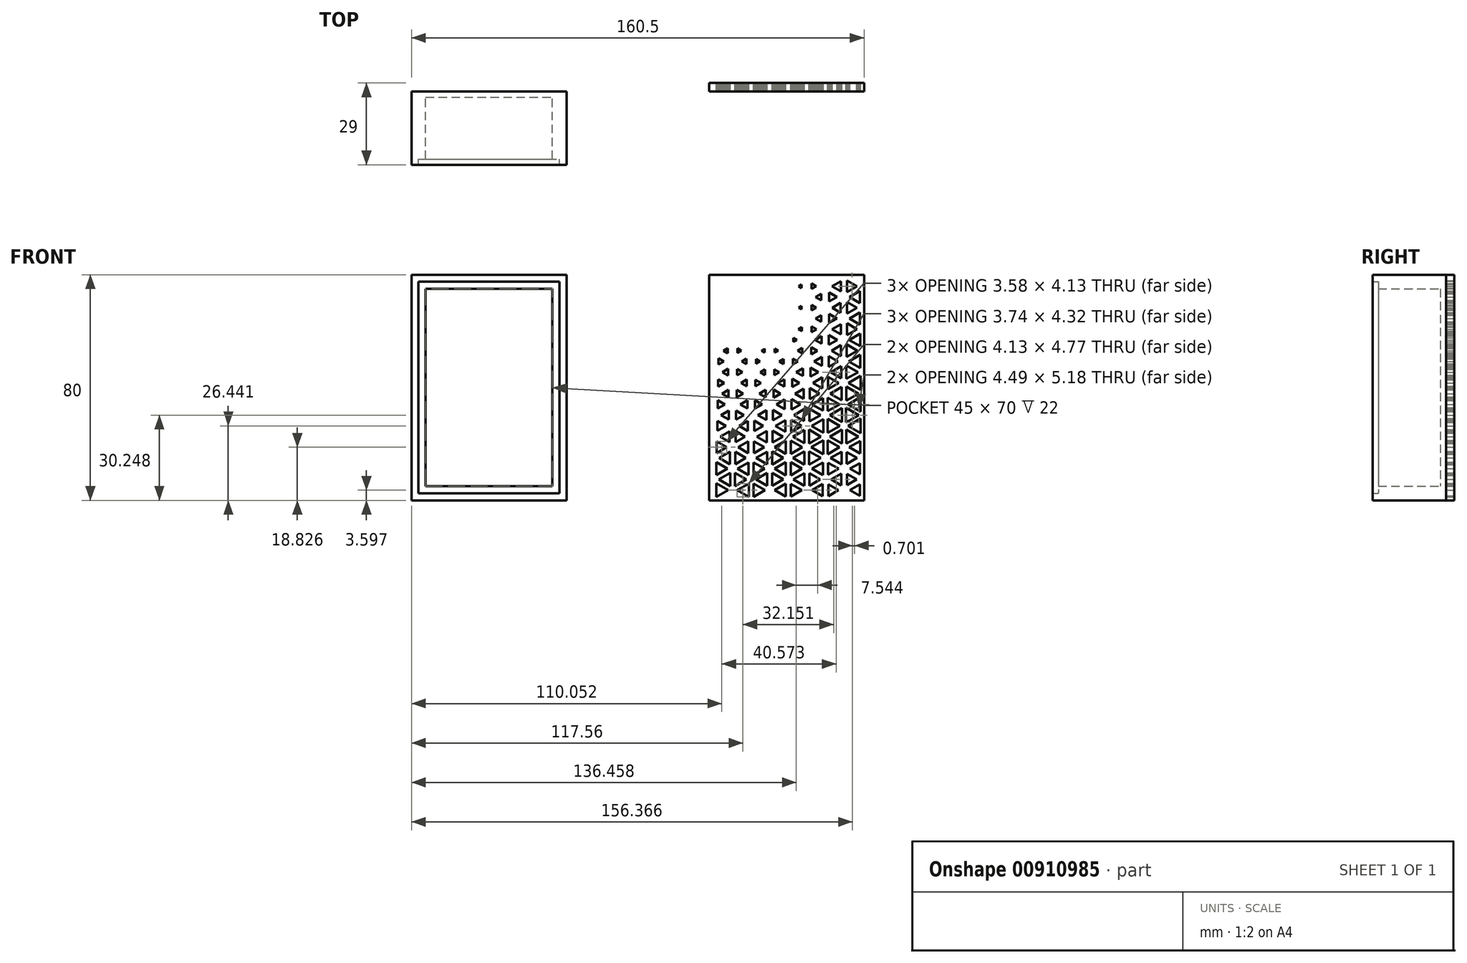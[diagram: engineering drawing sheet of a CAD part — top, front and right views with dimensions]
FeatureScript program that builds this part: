
annotation { "Feature Type Name" : "Feature", "Feature Type Description" : "" }
export const myFeature = defineFeature(function(context is Context, id is Id, definition is map)
    precondition{}
    {
        {
            var Q0;
            Q0=qCreatedBy(makeId("Front.planeOp"),FACE);
            var sketch = newSketch(context, id + "F0", { "sketchPlane" : qUnion([Q0])});
            skLineSegment(sketch, "E0.bottom", {"start": v(-84.52, 32) * mm, "end": v(-39.52, 32) * mm});
            skLineSegment(sketch, "E0.top", {"start": v(-84.52, -38) * mm, "end": v(-39.52, -38) * mm});
            skLineSegment(sketch, "E0.left", {"start": v(-84.52, 32) * mm, "end": v(-84.52, -38) * mm});
            skLineSegment(sketch, "E0.right", {"start": v(-39.52, 32) * mm, "end": v(-39.52, -38) * mm});
            skLineSegment(sketch, "E1.0", {"start": v(-89.52, 37) * mm, "end": v(-34.52, 37) * mm});
            skLineSegment(sketch, "E1.1", {"start": v(-89.52, 37) * mm, "end": v(-89.52, -43) * mm});
            skLineSegment(sketch, "E1.2", {"start": v(-89.52, -43) * mm, "end": v(-34.52, -43) * mm});
            skLineSegment(sketch, "E1.3", {"start": v(-34.52, 37) * mm, "end": v(-34.52, -43) * mm});
            skLineSegment(sketch, "E2.0", {"start": v(-37.02, 34.5) * mm, "end": v(-37.02, -40.5) * mm});
            skLineSegment(sketch, "E2.1", {"start": v(-87.02, 34.5) * mm, "end": v(-37.02, 34.5) * mm});
            skLineSegment(sketch, "E2.2", {"start": v(-87.02, 34.5) * mm, "end": v(-87.02, -40.5) * mm});
            skLineSegment(sketch, "E2.3", {"start": v(-87.02, -40.5) * mm, "end": v(-37.02, -40.5) * mm});
            skSolve(sketch);
        }
        {
            var Q0;
            Q0=makeQuery(id+"F0.imprint","IMPRINT",FACE,{"disambiguationData":[TD([[makeQuery(id+"F0.imprint","IMPRINT",EDGE,{"derivedFrom":sQuery(id+"F0.wireOp",EDGE,"E0.bottom")}),1.0]])]});
            extrude(context, id + "F1", {"entities" : qUnion([Q0]), "depth" : 22 * mm, "offsetDistance" : 25 * mm});
        }
        {
            var Q0;
            Q0=makeQuery(id+"F0.imprint","IMPRINT",FACE,{"disambiguationData":[TD([[makeQuery(id+"F0.imprint","IMPRINT",EDGE,{"derivedFrom":sQuery(id+"F0.wireOp",EDGE,"E1.0")}),-1.0]])]});
            extrude(context, id + "F2", {"entities" : qUnion([Q0]), "operationType" : NewBodyOperationType.ADD, "depth" : 24 * mm, "offsetDistance" : 25 * mm, "hasSecondDirection" : true, "secondDirectionOppositeDirection" : true, "secondDirectionDepth" : 2 * mm});
        }
        {
            var Q0;
            {var subQ0=sQuery(id+"F0.wireOp",EDGE,"E2.3");var subQ1=sQuery(id+"F0.wireOp",EDGE,"E2.2");var subQ2=sQuery(id+"F0.wireOp",EDGE,"E2.1");var subQ3=sQuery(id+"F0.wireOp",EDGE,"E2.0");Q0=makeQuery(id+"F2.boolean.opBoolean","SPLIT",FACE,{"disambiguationData":[TD([makeQuery(id+"F1.opExtrude","CAP_FACE",FACE,{"disambiguationData":[OSD([sQuery(id+"F0.wireOp",EDGE,"E0.bottom"),sQuery(id+"F0.wireOp",EDGE,"E0.top"),sQuery(id+"F0.wireOp",EDGE,"E0.left"),sQuery(id+"F0.wireOp",EDGE,"E0.right"),subQ3,subQ2,subQ1,subQ0])],"isStart":true})])],"derivedFrom":makeQuery(id+"F2.opExtrude","SWEPT_FACE",FACE,{"disambiguationData":[OSD([subQ1])]})});}
            extrude(context, id + "F3", {"entities" : qUnion([Q0]), "operationType" : NewBodyOperationType.ADD, "depth" : 51.4 * mm, "offsetDistance" : 25 * mm});
        }
        {
            var Q0;
            {var subQ0=sQuery(id+"F0.wireOp",EDGE,"E2.2");Q0=makeQuery(id+"F3.boolean.opBoolean","MERGE",FACE,{"derivedFrom":[makeQuery(id+"F2.opExtrude","CAP_FACE",FACE,{"disambiguationData":[OSD([sQuery(id+"F0.wireOp",EDGE,"E1.0"),sQuery(id+"F0.wireOp",EDGE,"E1.1"),sQuery(id+"F0.wireOp",EDGE,"E1.2"),sQuery(id+"F0.wireOp",EDGE,"E1.3"),sQuery(id+"F0.wireOp",EDGE,"E2.0"),sQuery(id+"F0.wireOp",EDGE,"E2.1"),subQ0,sQuery(id+"F0.wireOp",EDGE,"E2.3")])],"isStart":true}),makeQuery(id+"F3.opExtrude","SWEPT_FACE",FACE,{"disambiguationData":[OSD([subQ0]),TDD([makeQuery(id+"F2.opExtrude","CAP_EDGE",EDGE,{"disambiguationData":[OSD([subQ0])],"isStart":true})])]})]});}
            extrude(context, id + "F4", {"entities" : qUnion([Q0]), "depth" : 3 * mm, "offsetDistance" : 25 * mm});
        }
        {
            var Q0;
            Q0=makeQuery(id+"F4.opExtrude","SWEPT_BODY",BODY,{"disambiguationData":[OSD([sQuery(id+"F0.wireOp",EDGE,"E1.0"),sQuery(id+"F0.wireOp",EDGE,"E1.1"),sQuery(id+"F0.wireOp",EDGE,"E1.2"),sQuery(id+"F0.wireOp",EDGE,"E1.3"),sQuery(id+"F0.wireOp",EDGE,"E2.0"),sQuery(id+"F0.wireOp",EDGE,"E2.1"),sQuery(id+"F0.wireOp",EDGE,"E2.2"),sQuery(id+"F0.wireOp",EDGE,"E2.3")])]});
            transform(context, id + "F5", {"entities" : qUnion([Q0]), "transformType" : TransformType.TRANSLATION_3D, "dx" : 105.5 * mm, "dy" : 0 * mm, "dz" : 0 * mm, "makeCopy" : false});
        }
        {
            var Q0;
            Q0=makeQuery(id+"F4.opExtrude","CAP_FACE",FACE,{"disambiguationData":[OSD([sQuery(id+"F0.wireOp",EDGE,"E1.0"),sQuery(id+"F0.wireOp",EDGE,"E1.1"),sQuery(id+"F0.wireOp",EDGE,"E1.2"),sQuery(id+"F0.wireOp",EDGE,"E1.3"),sQuery(id+"F0.wireOp",EDGE,"E2.0"),sQuery(id+"F0.wireOp",EDGE,"E2.1"),sQuery(id+"F0.wireOp",EDGE,"E2.2"),sQuery(id+"F0.wireOp",EDGE,"E2.3")])],"isStart":false});
            var sketch = newSketch(context, id + "F6", { "sketchPlane" : qUnion([Q0])});
            skLineSegment(sketch, "E3", {"start": v(-19.2, -2.61) * mm, "end": v(-21.42, -1.33) * mm});
            skLineSegment(sketch, "E4", {"start": v(-21.42, -1.33) * mm, "end": v(-19.2, -0.05) * mm});
            skLineSegment(sketch, "E5", {"start": v(-19.2, -0.05) * mm, "end": v(-19.2, -2.61) * mm});
            skLineSegment(sketch, "E6", {"start": v(-19.3, 5.18) * mm, "end": v(-21.2, 6.29) * mm});
            skLineSegment(sketch, "E7", {"start": v(-21.2, 6.29) * mm, "end": v(-19.3, 7.39) * mm});
            skLineSegment(sketch, "E8", {"start": v(-19.3, 7.39) * mm, "end": v(-19.3, 5.18) * mm});
            skLineSegment(sketch, "E9", {"start": v(-20.78, 2.48) * mm, "end": v(-22.81, 1.3) * mm});
            skLineSegment(sketch, "E10", {"start": v(-22.81, 1.3) * mm, "end": v(-22.81, 3.65) * mm});
            skLineSegment(sketch, "E11", {"start": v(-22.81, 3.65) * mm, "end": v(-20.78, 2.48) * mm});
            skLineSegment(sketch, "E12", {"start": v(-20.58, -5.14) * mm, "end": v(-22.91, -6.49) * mm});
            skLineSegment(sketch, "E13", {"start": v(-22.91, -6.49) * mm, "end": v(-22.91, -3.79) * mm});
            skLineSegment(sketch, "E14", {"start": v(-22.91, -3.79) * mm, "end": v(-20.58, -5.14) * mm});
            skLineSegment(sketch, "E15", {"start": v(-21.1, 10.1) * mm, "end": v(-22.65, 9.2) * mm});
            skLineSegment(sketch, "E16", {"start": v(-22.65, 9.2) * mm, "end": v(-22.65, 11) * mm});
            skLineSegment(sketch, "E17", {"start": v(-22.65, 11) * mm, "end": v(-21.1, 10.1) * mm});
            skLineSegment(sketch, "E18", {"start": v(-25.9, 1.37) * mm, "end": v(-27.8, 2.48) * mm});
            skLineSegment(sketch, "E19", {"start": v(-27.8, 2.48) * mm, "end": v(-25.9, 3.58) * mm});
            skLineSegment(sketch, "E20", {"start": v(-25.9, 3.58) * mm, "end": v(-25.9, 1.37) * mm});
            skLineSegment(sketch, "E21", {"start": v(-19.09, -10.42) * mm, "end": v(-21.64, -8.94) * mm});
            skLineSegment(sketch, "E22", {"start": v(-21.64, -8.94) * mm, "end": v(-19.09, -7.47) * mm});
            skLineSegment(sketch, "E23", {"start": v(-19.09, -7.47) * mm, "end": v(-19.09, -10.42) * mm});
            skLineSegment(sketch, "E24", {"start": v(-26.06, 9.27) * mm, "end": v(-27.48, 10.1) * mm});
            skLineSegment(sketch, "E25", {"start": v(-27.48, 10.1) * mm, "end": v(-26.06, 10.91) * mm});
            skLineSegment(sketch, "E26", {"start": v(-26.06, 10.91) * mm, "end": v(-26.06, 9.27) * mm});
            skLineSegment(sketch, "E27", {"start": v(-27.65, 6.29) * mm, "end": v(-29.27, 5.35) * mm});
            skLineSegment(sketch, "E28", {"start": v(-29.27, 5.35) * mm, "end": v(-29.27, 7.22) * mm});
            skLineSegment(sketch, "E29", {"start": v(-29.27, 7.22) * mm, "end": v(-27.65, 6.29) * mm});
            skLineSegment(sketch, "E30", {"start": v(-27.37, -1.33) * mm, "end": v(-29.41, -2.51) * mm});
            skLineSegment(sketch, "E31", {"start": v(-29.41, -2.51) * mm, "end": v(-29.41, -0.15) * mm});
            skLineSegment(sketch, "E32", {"start": v(-29.41, -0.15) * mm, "end": v(-27.37, -1.33) * mm});
            skLineSegment(sketch, "E33", {"start": v(-25.76, -6.46) * mm, "end": v(-28.06, -5.14) * mm});
            skLineSegment(sketch, "E34", {"start": v(-28.06, -5.14) * mm, "end": v(-25.76, -3.8) * mm});
            skLineSegment(sketch, "E35", {"start": v(-25.76, -3.8) * mm, "end": v(-25.76, -6.46) * mm});
            skLineSegment(sketch, "E36", {"start": v(-25.6, -14.35) * mm, "end": v(-28.38, -12.75) * mm});
            skLineSegment(sketch, "E37", {"start": v(-28.38, -12.75) * mm, "end": v(-25.6, -11.15) * mm});
            skLineSegment(sketch, "E38", {"start": v(-25.6, -11.15) * mm, "end": v(-25.6, -14.35) * mm});
            skLineSegment(sketch, "E39", {"start": v(-20.28, -12.75) * mm, "end": v(-23.06, -14.36) * mm});
            skLineSegment(sketch, "E40", {"start": v(-23.06, -14.36) * mm, "end": v(-23.06, -11.15) * mm});
            skLineSegment(sketch, "E41", {"start": v(-23.06, -11.15) * mm, "end": v(-20.28, -12.75) * mm});
            skLineSegment(sketch, "E42", {"start": v(-32.63, 5.42) * mm, "end": v(-34.12, 6.29) * mm});
            skLineSegment(sketch, "E43", {"start": v(-34.12, 6.29) * mm, "end": v(-32.63, 7.15) * mm});
            skLineSegment(sketch, "E44", {"start": v(-32.63, 7.15) * mm, "end": v(-32.63, 5.42) * mm});
            skLineSegment(sketch, "E45", {"start": v(-34.17, 2.48) * mm, "end": v(-35.9, 1.48) * mm});
            skLineSegment(sketch, "E46", {"start": v(-35.9, 1.48) * mm, "end": v(-35.9, 3.48) * mm});
            skLineSegment(sketch, "E47", {"start": v(-35.9, 3.48) * mm, "end": v(-34.17, 2.48) * mm});
            skLineSegment(sketch, "E48", {"start": v(-32.46, -2.49) * mm, "end": v(-34.46, -1.33) * mm});
            skLineSegment(sketch, "E49", {"start": v(-34.46, -1.33) * mm, "end": v(-32.46, -0.17) * mm});
            skLineSegment(sketch, "E50", {"start": v(-32.46, -0.17) * mm, "end": v(-32.46, -2.49) * mm});
            skLineSegment(sketch, "E51", {"start": v(-27.04, -8.94) * mm, "end": v(-29.58, -10.41) * mm});
            skLineSegment(sketch, "E52", {"start": v(-29.58, -10.41) * mm, "end": v(-29.58, -7.48) * mm});
            skLineSegment(sketch, "E53", {"start": v(-29.58, -7.48) * mm, "end": v(-27.04, -8.94) * mm});
            skLineSegment(sketch, "E54", {"start": v(-26.67, -16.56) * mm, "end": v(-29.76, -18.34) * mm});
            skLineSegment(sketch, "E55", {"start": v(-29.76, -18.34) * mm, "end": v(-29.76, -14.78) * mm});
            skLineSegment(sketch, "E56", {"start": v(-29.76, -14.78) * mm, "end": v(-26.67, -16.56) * mm});
            skLineSegment(sketch, "E57", {"start": v(-18.92, -18.31) * mm, "end": v(-21.96, -16.56) * mm});
            skLineSegment(sketch, "E58", {"start": v(-21.96, -16.56) * mm, "end": v(-18.92, -14.8) * mm});
            skLineSegment(sketch, "E59", {"start": v(-18.92, -14.8) * mm, "end": v(-18.92, -18.31) * mm});
            skLineSegment(sketch, "E60", {"start": v(-34.54, 10.1) * mm, "end": v(-35.72, 9.4) * mm});
            skLineSegment(sketch, "E61", {"start": v(-35.72, 9.4) * mm, "end": v(-35.72, 10.78) * mm});
            skLineSegment(sketch, "E62", {"start": v(-35.72, 10.78) * mm, "end": v(-34.54, 10.1) * mm});
            skLineSegment(sketch, "E63", {"start": v(-39.13, 1.46) * mm, "end": v(-40.9, 2.48) * mm});
            skLineSegment(sketch, "E64", {"start": v(-40.9, 2.48) * mm, "end": v(-39.13, 3.5) * mm});
            skLineSegment(sketch, "E65", {"start": v(-39.13, 3.5) * mm, "end": v(-39.13, 1.46) * mm});
            skLineSegment(sketch, "E66", {"start": v(-33.77, -5.14) * mm, "end": v(-36.1, -6.49) * mm});
            skLineSegment(sketch, "E67", {"start": v(-36.1, -6.49) * mm, "end": v(-36.1, -3.79) * mm});
            skLineSegment(sketch, "E68", {"start": v(-36.1, -3.79) * mm, "end": v(-33.77, -5.14) * mm});
            skLineSegment(sketch, "E69", {"start": v(-32.26, -10.44) * mm, "end": v(-34.85, -8.94) * mm});
            skLineSegment(sketch, "E70", {"start": v(-34.85, -8.94) * mm, "end": v(-32.26, -7.45) * mm});
            skLineSegment(sketch, "E71", {"start": v(-32.26, -7.45) * mm, "end": v(-32.26, -10.44) * mm});
            skLineSegment(sketch, "E72", {"start": v(-25.42, -22.28) * mm, "end": v(-28.74, -20.37) * mm});
            skLineSegment(sketch, "E73", {"start": v(-28.74, -20.37) * mm, "end": v(-25.42, -18.45) * mm});
            skLineSegment(sketch, "E74", {"start": v(-25.42, -18.45) * mm, "end": v(-25.42, -22.28) * mm});
            skLineSegment(sketch, "E75", {"start": v(-19.94, -20.37) * mm, "end": v(-23.23, -22.27) * mm});
            skLineSegment(sketch, "E76", {"start": v(-23.23, -22.27) * mm, "end": v(-23.23, -18.46) * mm});
            skLineSegment(sketch, "E77", {"start": v(-23.23, -18.46) * mm, "end": v(-19.94, -20.37) * mm});
            skLineSegment(sketch, "E78", {"start": v(-39.33, 9.41) * mm, "end": v(-40.5, 10.1) * mm});
            skLineSegment(sketch, "E79", {"start": v(-40.5, 10.1) * mm, "end": v(-39.33, 10.77) * mm});
            skLineSegment(sketch, "E80", {"start": v(-39.33, 10.77) * mm, "end": v(-39.33, 9.41) * mm});
            skLineSegment(sketch, "E81", {"start": v(-40.9, 6.29) * mm, "end": v(-42.43, 5.4) * mm});
            skLineSegment(sketch, "E82", {"start": v(-42.43, 5.4) * mm, "end": v(-42.43, 7.16) * mm});
            skLineSegment(sketch, "E83", {"start": v(-42.43, 7.16) * mm, "end": v(-40.9, 6.29) * mm});
            skLineSegment(sketch, "E84", {"start": v(-40.44, -1.33) * mm, "end": v(-42.66, -2.61) * mm});
            skLineSegment(sketch, "E85", {"start": v(-42.66, -2.61) * mm, "end": v(-42.66, -0.05) * mm});
            skLineSegment(sketch, "E86", {"start": v(-42.66, -0.05) * mm, "end": v(-40.44, -1.33) * mm});
            skLineSegment(sketch, "E87", {"start": v(-38.9, -6.57) * mm, "end": v(-41.37, -5.14) * mm});
            skLineSegment(sketch, "E88", {"start": v(-41.37, -5.14) * mm, "end": v(-38.9, -3.7) * mm});
            skLineSegment(sketch, "E89", {"start": v(-38.9, -3.7) * mm, "end": v(-38.9, -6.57) * mm});
            skLineSegment(sketch, "E90", {"start": v(-33.35, -12.75) * mm, "end": v(-36.31, -14.46) * mm});
            skLineSegment(sketch, "E91", {"start": v(-36.31, -14.46) * mm, "end": v(-36.31, -11.04) * mm});
            skLineSegment(sketch, "E92", {"start": v(-36.31, -11.04) * mm, "end": v(-33.35, -12.75) * mm});
            skLineSegment(sketch, "E93", {"start": v(-32.07, -18.39) * mm, "end": v(-35.24, -16.56) * mm});
            skLineSegment(sketch, "E94", {"start": v(-35.24, -16.56) * mm, "end": v(-32.07, -14.73) * mm});
            skLineSegment(sketch, "E95", {"start": v(-32.07, -14.73) * mm, "end": v(-32.07, -18.39) * mm});
            skLineSegment(sketch, "E96", {"start": v(-31.9, -26.3) * mm, "end": v(-35.59, -24.17) * mm});
            skLineSegment(sketch, "E97", {"start": v(-35.59, -24.17) * mm, "end": v(-31.9, -22.04) * mm});
            skLineSegment(sketch, "E98", {"start": v(-31.9, -22.04) * mm, "end": v(-31.9, -26.3) * mm});
            skLineSegment(sketch, "E99", {"start": v(-26.32, -24.17) * mm, "end": v(-29.93, -26.26) * mm});
            skLineSegment(sketch, "E100", {"start": v(-29.93, -26.26) * mm, "end": v(-29.93, -22.1) * mm});
            skLineSegment(sketch, "E101", {"start": v(-29.93, -22.1) * mm, "end": v(-26.32, -24.17) * mm});
            skLineSegment(sketch, "E102", {"start": v(-18.74, -26.24) * mm, "end": v(-22.32, -24.17) * mm});
            skLineSegment(sketch, "E103", {"start": v(-22.32, -24.17) * mm, "end": v(-18.74, -22.1) * mm});
            skLineSegment(sketch, "E104", {"start": v(-18.74, -22.1) * mm, "end": v(-18.74, -26.24) * mm});
            skLineSegment(sketch, "E105", {"start": v(-45.72, 5.25) * mm, "end": v(-47.51, 6.29) * mm});
            skLineSegment(sketch, "E106", {"start": v(-47.51, 6.29) * mm, "end": v(-45.72, 7.32) * mm});
            skLineSegment(sketch, "E107", {"start": v(-45.72, 7.32) * mm, "end": v(-45.72, 5.25) * mm});
            skLineSegment(sketch, "E108", {"start": v(-46.95, 2.48) * mm, "end": v(-49.3, 1.12) * mm});
            skLineSegment(sketch, "E109", {"start": v(-49.3, 1.12) * mm, "end": v(-49.3, 3.83) * mm});
            skLineSegment(sketch, "E110", {"start": v(-49.3, 3.83) * mm, "end": v(-46.95, 2.48) * mm});
            skLineSegment(sketch, "E111", {"start": v(-45.48, -2.78) * mm, "end": v(-47.99, -1.33) * mm});
            skLineSegment(sketch, "E112", {"start": v(-47.99, -1.33) * mm, "end": v(-45.48, 0.12) * mm});
            skLineSegment(sketch, "E113", {"start": v(-45.48, 0.12) * mm, "end": v(-45.48, -2.78) * mm});
            skLineSegment(sketch, "E114", {"start": v(-39.96, -8.94) * mm, "end": v(-42.9, -10.64) * mm});
            skLineSegment(sketch, "E115", {"start": v(-42.9, -10.64) * mm, "end": v(-42.9, -7.25) * mm});
            skLineSegment(sketch, "E116", {"start": v(-42.9, -7.25) * mm, "end": v(-39.96, -8.94) * mm});
            skLineSegment(sketch, "E117", {"start": v(-38.68, -14.56) * mm, "end": v(-41.8, -12.75) * mm});
            skLineSegment(sketch, "E118", {"start": v(-41.8, -12.75) * mm, "end": v(-38.68, -10.95) * mm});
            skLineSegment(sketch, "E119", {"start": v(-38.68, -10.95) * mm, "end": v(-38.68, -14.56) * mm});
            skLineSegment(sketch, "E120", {"start": v(-32.98, -20.37) * mm, "end": v(-36.5, -22.4) * mm});
            skLineSegment(sketch, "E121", {"start": v(-36.5, -22.4) * mm, "end": v(-36.5, -18.33) * mm});
            skLineSegment(sketch, "E122", {"start": v(-36.5, -18.33) * mm, "end": v(-32.98, -20.37) * mm});
            skLineSegment(sketch, "E123", {"start": v(-32.73, -27.98) * mm, "end": v(-36.62, -30.22) * mm});
            skLineSegment(sketch, "E124", {"start": v(-36.62, -30.22) * mm, "end": v(-36.62, -25.74) * mm});
            skLineSegment(sketch, "E125", {"start": v(-36.62, -25.74) * mm, "end": v(-32.73, -27.98) * mm});
            skLineSegment(sketch, "E126", {"start": v(-25.27, -30.17) * mm, "end": v(-29.05, -27.98) * mm});
            skLineSegment(sketch, "E127", {"start": v(-29.05, -27.98) * mm, "end": v(-25.27, -25.8) * mm});
            skLineSegment(sketch, "E128", {"start": v(-25.27, -25.8) * mm, "end": v(-25.27, -30.17) * mm});
            skLineSegment(sketch, "E129", {"start": v(-19.62, -27.98) * mm, "end": v(-23.39, -30.16) * mm});
            skLineSegment(sketch, "E130", {"start": v(-23.39, -30.16) * mm, "end": v(-23.39, -25.8) * mm});
            skLineSegment(sketch, "E131", {"start": v(-23.39, -25.8) * mm, "end": v(-19.62, -27.98) * mm});
            skLineSegment(sketch, "E132", {"start": v(-45.9, 13.19) * mm, "end": v(-47.14, 13.9) * mm});
            skLineSegment(sketch, "E133", {"start": v(-47.14, 13.9) * mm, "end": v(-45.9, 14.61) * mm});
            skLineSegment(sketch, "E134", {"start": v(-45.9, 14.61) * mm, "end": v(-45.9, 13.19) * mm});
            skLineSegment(sketch, "E135", {"start": v(-47.39, 10.1) * mm, "end": v(-49.08, 9.12) * mm});
            skLineSegment(sketch, "E136", {"start": v(-49.08, 9.12) * mm, "end": v(-49.08, 11.07) * mm});
            skLineSegment(sketch, "E137", {"start": v(-49.08, 11.07) * mm, "end": v(-47.39, 10.1) * mm});
            skLineSegment(sketch, "E138", {"start": v(-51.98, 0.87) * mm, "end": v(-54.77, 2.48) * mm});
            skLineSegment(sketch, "E139", {"start": v(-54.77, 2.48) * mm, "end": v(-51.98, 4.09) * mm});
            skLineSegment(sketch, "E140", {"start": v(-51.98, 4.09) * mm, "end": v(-51.98, 0.87) * mm});
            skLineSegment(sketch, "E141", {"start": v(-46.47, -5.14) * mm, "end": v(-49.54, -6.9) * mm});
            skLineSegment(sketch, "E142", {"start": v(-49.54, -6.9) * mm, "end": v(-49.54, -3.37) * mm});
            skLineSegment(sketch, "E143", {"start": v(-49.54, -3.37) * mm, "end": v(-46.47, -5.14) * mm});
            skLineSegment(sketch, "E144", {"start": v(-45.24, -10.8) * mm, "end": v(-48.45, -8.94) * mm});
            skLineSegment(sketch, "E145", {"start": v(-48.45, -8.94) * mm, "end": v(-45.24, -7.1) * mm});
            skLineSegment(sketch, "E146", {"start": v(-45.24, -7.1) * mm, "end": v(-45.24, -10.8) * mm});
            skLineSegment(sketch, "E147", {"start": v(-39.57, -16.56) * mm, "end": v(-43.09, -18.59) * mm});
            skLineSegment(sketch, "E148", {"start": v(-43.09, -18.59) * mm, "end": v(-43.09, -14.53) * mm});
            skLineSegment(sketch, "E149", {"start": v(-43.09, -14.53) * mm, "end": v(-39.57, -16.56) * mm});
            skLineSegment(sketch, "E150", {"start": v(-38.5, -22.5) * mm, "end": v(-42.18, -20.37) * mm});
            skLineSegment(sketch, "E151", {"start": v(-42.18, -20.37) * mm, "end": v(-38.5, -18.24) * mm});
            skLineSegment(sketch, "E152", {"start": v(-38.5, -18.24) * mm, "end": v(-38.5, -22.5) * mm});
            skLineSegment(sketch, "E153", {"start": v(-31.82, -34.05) * mm, "end": v(-35.74, -31.79) * mm});
            skLineSegment(sketch, "E154", {"start": v(-35.74, -31.79) * mm, "end": v(-31.82, -29.53) * mm});
            skLineSegment(sketch, "E155", {"start": v(-31.82, -29.53) * mm, "end": v(-31.82, -34.05) * mm});
            skLineSegment(sketch, "E156", {"start": v(-26.13, -31.79) * mm, "end": v(-30.03, -34.04) * mm});
            skLineSegment(sketch, "E157", {"start": v(-30.03, -34.04) * mm, "end": v(-30.03, -29.54) * mm});
            skLineSegment(sketch, "E158", {"start": v(-30.03, -29.54) * mm, "end": v(-26.13, -31.79) * mm});
            skLineSegment(sketch, "E159", {"start": v(-18.62, -34.07) * mm, "end": v(-22.57, -31.79) * mm});
            skLineSegment(sketch, "E160", {"start": v(-22.57, -31.79) * mm, "end": v(-18.62, -29.5) * mm});
            skLineSegment(sketch, "E161", {"start": v(-18.62, -29.5) * mm, "end": v(-18.62, -34.07) * mm});
            skLineSegment(sketch, "E162", {"start": v(-47.68, 17.7) * mm, "end": v(-48.93, 16.98) * mm});
            skLineSegment(sketch, "E163", {"start": v(-48.93, 16.98) * mm, "end": v(-48.93, 18.43) * mm});
            skLineSegment(sketch, "E164", {"start": v(-48.93, 18.43) * mm, "end": v(-47.68, 17.7) * mm});
            skLineSegment(sketch, "E165", {"start": v(-52.18, 8.82) * mm, "end": v(-54.37, 10.1) * mm});
            skLineSegment(sketch, "E166", {"start": v(-54.37, 10.1) * mm, "end": v(-52.18, 11.36) * mm});
            skLineSegment(sketch, "E167", {"start": v(-52.18, 11.36) * mm, "end": v(-52.18, 8.82) * mm});
            skLineSegment(sketch, "E168", {"start": v(-53.27, 6.29) * mm, "end": v(-56.03, 4.7) * mm});
            skLineSegment(sketch, "E169", {"start": v(-56.03, 4.7) * mm, "end": v(-56.03, 7.88) * mm});
            skLineSegment(sketch, "E170", {"start": v(-56.03, 7.88) * mm, "end": v(-53.27, 6.29) * mm});
            skLineSegment(sketch, "E171", {"start": v(-52.89, -1.33) * mm, "end": v(-56.22, -3.25) * mm});
            skLineSegment(sketch, "E172", {"start": v(-56.22, -3.25) * mm, "end": v(-56.22, 0.6) * mm});
            skLineSegment(sketch, "E173", {"start": v(-56.22, 0.6) * mm, "end": v(-52.89, -1.33) * mm});
            skLineSegment(sketch, "E174", {"start": v(-51.76, -7.12) * mm, "end": v(-55.2, -5.14) * mm});
            skLineSegment(sketch, "E175", {"start": v(-55.2, -5.14) * mm, "end": v(-51.76, -3.16) * mm});
            skLineSegment(sketch, "E176", {"start": v(-51.76, -3.16) * mm, "end": v(-51.76, -7.12) * mm});
            skLineSegment(sketch, "E177", {"start": v(-46.1, -12.75) * mm, "end": v(-49.72, -14.85) * mm});
            skLineSegment(sketch, "E178", {"start": v(-49.72, -14.85) * mm, "end": v(-49.72, -10.65) * mm});
            skLineSegment(sketch, "E179", {"start": v(-49.72, -10.65) * mm, "end": v(-46.1, -12.75) * mm});
            skLineSegment(sketch, "E180", {"start": v(-45.07, -18.72) * mm, "end": v(-48.81, -16.56) * mm});
            skLineSegment(sketch, "E181", {"start": v(-48.81, -16.56) * mm, "end": v(-45.07, -14.4) * mm});
            skLineSegment(sketch, "E182", {"start": v(-45.07, -14.4) * mm, "end": v(-45.07, -18.72) * mm});
            skLineSegment(sketch, "E183", {"start": v(-39.27, -24.17) * mm, "end": v(-43.24, -26.46) * mm});
            skLineSegment(sketch, "E184", {"start": v(-43.24, -26.46) * mm, "end": v(-43.24, -21.88) * mm});
            skLineSegment(sketch, "E185", {"start": v(-43.24, -21.88) * mm, "end": v(-39.27, -24.17) * mm});
            skLineSegment(sketch, "E186", {"start": v(-38.4, -30.28) * mm, "end": v(-42.38, -27.98) * mm});
            skLineSegment(sketch, "E187", {"start": v(-42.38, -27.98) * mm, "end": v(-38.4, -25.68) * mm});
            skLineSegment(sketch, "E188", {"start": v(-38.4, -25.68) * mm, "end": v(-38.4, -30.28) * mm});
            skLineSegment(sketch, "E189", {"start": v(-38.4, -37.87) * mm, "end": v(-42.35, -35.6) * mm});
            skLineSegment(sketch, "E190", {"start": v(-42.35, -35.6) * mm, "end": v(-38.4, -33.32) * mm});
            skLineSegment(sketch, "E191", {"start": v(-38.4, -33.32) * mm, "end": v(-38.4, -37.87) * mm});
            skLineSegment(sketch, "E192", {"start": v(-32.68, -35.6) * mm, "end": v(-36.65, -37.89) * mm});
            skLineSegment(sketch, "E193", {"start": v(-36.65, -37.89) * mm, "end": v(-36.65, -33.3) * mm});
            skLineSegment(sketch, "E194", {"start": v(-36.65, -33.3) * mm, "end": v(-32.68, -35.6) * mm});
            skLineSegment(sketch, "E195", {"start": v(-25.19, -37.92) * mm, "end": v(-29.22, -35.6) * mm});
            skLineSegment(sketch, "E196", {"start": v(-29.22, -35.6) * mm, "end": v(-25.19, -33.27) * mm});
            skLineSegment(sketch, "E197", {"start": v(-25.19, -33.27) * mm, "end": v(-25.19, -37.92) * mm});
            skLineSegment(sketch, "E198", {"start": v(-19.42, -35.6) * mm, "end": v(-23.49, -37.94) * mm});
            skLineSegment(sketch, "E199", {"start": v(-23.49, -37.94) * mm, "end": v(-23.49, -33.25) * mm});
            skLineSegment(sketch, "E200", {"start": v(-23.49, -33.25) * mm, "end": v(-19.42, -35.6) * mm});
            skLineSegment(sketch, "E201", {"start": v(-47.83, 25.32) * mm, "end": v(-48.85, 24.73) * mm});
            skLineSegment(sketch, "E202", {"start": v(-48.85, 24.73) * mm, "end": v(-48.85, 25.91) * mm});
            skLineSegment(sketch, "E203", {"start": v(-48.85, 25.91) * mm, "end": v(-47.83, 25.32) * mm});
            skLineSegment(sketch, "E204", {"start": v(-52.31, 16.68) * mm, "end": v(-54.1, 17.7) * mm});
            skLineSegment(sketch, "E205", {"start": v(-54.1, 17.7) * mm, "end": v(-52.31, 18.74) * mm});
            skLineSegment(sketch, "E206", {"start": v(-52.31, 18.74) * mm, "end": v(-52.31, 16.68) * mm});
            skLineSegment(sketch, "E207", {"start": v(-53.59, 13.9) * mm, "end": v(-55.87, 12.59) * mm});
            skLineSegment(sketch, "E208", {"start": v(-55.87, 12.59) * mm, "end": v(-55.87, 15.21) * mm});
            skLineSegment(sketch, "E209", {"start": v(-55.87, 15.21) * mm, "end": v(-53.59, 13.9) * mm});
            skLineSegment(sketch, "E210", {"start": v(-58.4, 4.37) * mm, "end": v(-61.72, 6.29) * mm});
            skLineSegment(sketch, "E211", {"start": v(-61.72, 6.29) * mm, "end": v(-58.4, 8.2) * mm});
            skLineSegment(sketch, "E212", {"start": v(-58.4, 8.2) * mm, "end": v(-58.4, 4.37) * mm});
            skLineSegment(sketch, "E213", {"start": v(-59.2, 2.48) * mm, "end": v(-62.95, 0.32) * mm});
            skLineSegment(sketch, "E214", {"start": v(-62.95, 0.32) * mm, "end": v(-62.95, 4.64) * mm});
            skLineSegment(sketch, "E215", {"start": v(-62.95, 4.64) * mm, "end": v(-59.2, 2.48) * mm});
            skLineSegment(sketch, "E216", {"start": v(-58.25, -3.5) * mm, "end": v(-62, -1.33) * mm});
            skLineSegment(sketch, "E217", {"start": v(-62, -1.33) * mm, "end": v(-58.25, 0.84) * mm});
            skLineSegment(sketch, "E218", {"start": v(-58.25, 0.84) * mm, "end": v(-58.25, -3.5) * mm});
            skLineSegment(sketch, "E219", {"start": v(-52.54, -8.94) * mm, "end": v(-56.39, -11.16) * mm});
            skLineSegment(sketch, "E220", {"start": v(-56.39, -11.16) * mm, "end": v(-56.39, -6.73) * mm});
            skLineSegment(sketch, "E221", {"start": v(-56.39, -6.73) * mm, "end": v(-52.54, -8.94) * mm});
            skLineSegment(sketch, "E222", {"start": v(-51.6, -15.01) * mm, "end": v(-55.52, -12.75) * mm});
            skLineSegment(sketch, "E223", {"start": v(-55.52, -12.75) * mm, "end": v(-51.6, -10.5) * mm});
            skLineSegment(sketch, "E224", {"start": v(-51.6, -10.5) * mm, "end": v(-51.6, -15.01) * mm});
            skLineSegment(sketch, "E225", {"start": v(-45.81, -20.37) * mm, "end": v(-49.86, -22.7) * mm});
            skLineSegment(sketch, "E226", {"start": v(-49.86, -22.7) * mm, "end": v(-49.86, -18.03) * mm});
            skLineSegment(sketch, "E227", {"start": v(-49.86, -18.03) * mm, "end": v(-45.81, -20.37) * mm});
            skLineSegment(sketch, "E228", {"start": v(-44.95, -26.54) * mm, "end": v(-49.04, -24.17) * mm});
            skLineSegment(sketch, "E229", {"start": v(-49.04, -24.17) * mm, "end": v(-44.95, -21.81) * mm});
            skLineSegment(sketch, "E230", {"start": v(-44.95, -21.81) * mm, "end": v(-44.95, -26.54) * mm});
            skLineSegment(sketch, "E231", {"start": v(-39.25, -31.79) * mm, "end": v(-43.25, -34.1) * mm});
            skLineSegment(sketch, "E232", {"start": v(-43.25, -34.1) * mm, "end": v(-43.25, -29.48) * mm});
            skLineSegment(sketch, "E233", {"start": v(-43.25, -29.48) * mm, "end": v(-39.25, -31.79) * mm});
            skLineSegment(sketch, "E234", {"start": v(-39.28, -39.4) * mm, "end": v(-43.23, -41.68) * mm});
            skLineSegment(sketch, "E235", {"start": v(-43.23, -41.68) * mm, "end": v(-43.23, -37.12) * mm});
            skLineSegment(sketch, "E236", {"start": v(-43.23, -37.12) * mm, "end": v(-39.28, -39.4) * mm});
            skLineSegment(sketch, "E237", {"start": v(-31.77, -41.76) * mm, "end": v(-35.84, -39.4) * mm});
            skLineSegment(sketch, "E238", {"start": v(-35.84, -39.4) * mm, "end": v(-31.77, -37.05) * mm});
            skLineSegment(sketch, "E239", {"start": v(-31.77, -37.05) * mm, "end": v(-31.77, -41.76) * mm});
            skLineSegment(sketch, "E240", {"start": v(-25.98, -39.4) * mm, "end": v(-30.1, -41.79) * mm});
            skLineSegment(sketch, "E241", {"start": v(-30.1, -41.79) * mm, "end": v(-30.1, -37.02) * mm});
            skLineSegment(sketch, "E242", {"start": v(-30.1, -37.02) * mm, "end": v(-25.98, -39.4) * mm});
            skLineSegment(sketch, "E243", {"start": v(-18.55, -41.8) * mm, "end": v(-22.71, -39.4) * mm});
            skLineSegment(sketch, "E244", {"start": v(-22.71, -39.4) * mm, "end": v(-18.55, -37) * mm});
            skLineSegment(sketch, "E245", {"start": v(-18.55, -37) * mm, "end": v(-18.55, -41.8) * mm});
            skLineSegment(sketch, "E246", {"start": v(-47.8, 32.94) * mm, "end": v(-48.87, 32.32) * mm});
            skLineSegment(sketch, "E247", {"start": v(-48.87, 32.32) * mm, "end": v(-48.87, 33.55) * mm});
            skLineSegment(sketch, "E248", {"start": v(-48.87, 33.55) * mm, "end": v(-47.8, 32.94) * mm});
            skLineSegment(sketch, "E249", {"start": v(-52.38, 24.4) * mm, "end": v(-53.97, 25.32) * mm});
            skLineSegment(sketch, "E250", {"start": v(-53.97, 25.32) * mm, "end": v(-52.38, 26.25) * mm});
            skLineSegment(sketch, "E251", {"start": v(-52.38, 26.25) * mm, "end": v(-52.38, 24.4) * mm});
            skLineSegment(sketch, "E252", {"start": v(-53.77, 21.52) * mm, "end": v(-55.77, 20.36) * mm});
            skLineSegment(sketch, "E253", {"start": v(-55.77, 20.36) * mm, "end": v(-55.77, 22.67) * mm});
            skLineSegment(sketch, "E254", {"start": v(-55.77, 22.67) * mm, "end": v(-53.77, 21.52) * mm});
            skLineSegment(sketch, "E255", {"start": v(-58.52, 12.2) * mm, "end": v(-61.47, 13.9) * mm});
            skLineSegment(sketch, "E256", {"start": v(-61.47, 13.9) * mm, "end": v(-58.52, 15.6) * mm});
            skLineSegment(sketch, "E257", {"start": v(-58.52, 15.6) * mm, "end": v(-58.52, 12.2) * mm});
            skLineSegment(sketch, "E258", {"start": v(-59.45, 10.1) * mm, "end": v(-62.83, 8.14) * mm});
            skLineSegment(sketch, "E259", {"start": v(-62.83, 8.14) * mm, "end": v(-62.83, 12.04) * mm});
            skLineSegment(sketch, "E260", {"start": v(-62.83, 12.04) * mm, "end": v(-59.45, 10.1) * mm});
            skLineSegment(sketch, "E261", {"start": v(-64.74, 0.12) * mm, "end": v(-68.82, 2.48) * mm});
            skLineSegment(sketch, "E262", {"start": v(-68.82, 2.48) * mm, "end": v(-64.74, 4.83) * mm});
            skLineSegment(sketch, "E263", {"start": v(-64.74, 4.83) * mm, "end": v(-64.74, 0.12) * mm});
            skLineSegment(sketch, "E264", {"start": v(-58.96, -5.14) * mm, "end": v(-63.07, -7.51) * mm});
            skLineSegment(sketch, "E265", {"start": v(-63.07, -7.51) * mm, "end": v(-63.07, -2.76) * mm});
            skLineSegment(sketch, "E266", {"start": v(-63.07, -2.76) * mm, "end": v(-58.96, -5.14) * mm});
            skLineSegment(sketch, "E267", {"start": v(-58.13, -11.33) * mm, "end": v(-62.26, -8.94) * mm});
            skLineSegment(sketch, "E268", {"start": v(-62.26, -8.94) * mm, "end": v(-58.13, -6.56) * mm});
            skLineSegment(sketch, "E269", {"start": v(-58.13, -6.56) * mm, "end": v(-58.13, -11.33) * mm});
            skLineSegment(sketch, "E270", {"start": v(-52.32, -16.56) * mm, "end": v(-56.5, -18.97) * mm});
            skLineSegment(sketch, "E271", {"start": v(-56.5, -18.97) * mm, "end": v(-56.5, -14.14) * mm});
            skLineSegment(sketch, "E272", {"start": v(-56.5, -14.14) * mm, "end": v(-52.32, -16.56) * mm});
            skLineSegment(sketch, "E273", {"start": v(-51.5, -22.8) * mm, "end": v(-55.71, -20.37) * mm});
            skLineSegment(sketch, "E274", {"start": v(-55.71, -20.37) * mm, "end": v(-51.5, -17.94) * mm});
            skLineSegment(sketch, "E275", {"start": v(-51.5, -17.94) * mm, "end": v(-51.5, -22.8) * mm});
            skLineSegment(sketch, "E276", {"start": v(-45.77, -27.98) * mm, "end": v(-49.88, -30.36) * mm});
            skLineSegment(sketch, "E277", {"start": v(-49.88, -30.36) * mm, "end": v(-49.88, -25.6) * mm});
            skLineSegment(sketch, "E278", {"start": v(-49.88, -25.6) * mm, "end": v(-45.77, -27.98) * mm});
            skLineSegment(sketch, "E279", {"start": v(-44.98, -34.1) * mm, "end": v(-48.98, -31.79) * mm});
            skLineSegment(sketch, "E280", {"start": v(-48.98, -31.79) * mm, "end": v(-44.98, -29.48) * mm});
            skLineSegment(sketch, "E281", {"start": v(-44.98, -29.48) * mm, "end": v(-44.98, -34.1) * mm});
            skLineSegment(sketch, "E282", {"start": v(-38.36, -45.56) * mm, "end": v(-42.43, -43.21) * mm});
            skLineSegment(sketch, "E283", {"start": v(-42.43, -43.21) * mm, "end": v(-38.36, -40.86) * mm});
            skLineSegment(sketch, "E284", {"start": v(-38.36, -40.86) * mm, "end": v(-38.36, -45.56) * mm});
            skLineSegment(sketch, "E285", {"start": v(-32.57, -43.21) * mm, "end": v(-36.7, -45.6) * mm});
            skLineSegment(sketch, "E286", {"start": v(-36.7, -45.6) * mm, "end": v(-36.7, -40.82) * mm});
            skLineSegment(sketch, "E287", {"start": v(-36.7, -40.82) * mm, "end": v(-32.57, -43.21) * mm});
            skLineSegment(sketch, "E288", {"start": v(-25.1, -45.67) * mm, "end": v(-29.37, -43.21) * mm});
            skLineSegment(sketch, "E289", {"start": v(-29.37, -43.21) * mm, "end": v(-25.1, -40.75) * mm});
            skLineSegment(sketch, "E290", {"start": v(-25.1, -40.75) * mm, "end": v(-25.1, -45.67) * mm});
            skLineSegment(sketch, "E291", {"start": v(-19.3, -43.21) * mm, "end": v(-23.55, -45.66) * mm});
            skLineSegment(sketch, "E292", {"start": v(-23.55, -45.66) * mm, "end": v(-23.55, -40.76) * mm});
            skLineSegment(sketch, "E293", {"start": v(-23.55, -40.76) * mm, "end": v(-19.3, -43.21) * mm});
            skLineSegment(sketch, "E294", {"start": v(-45.86, 43.58) * mm, "end": v(-47.21, 44.36) * mm});
            skLineSegment(sketch, "E295", {"start": v(-47.21, 44.36) * mm, "end": v(-45.86, 45.14) * mm});
            skLineSegment(sketch, "E296", {"start": v(-45.86, 45.14) * mm, "end": v(-45.86, 43.58) * mm});
            skLineSegment(sketch, "E297", {"start": v(-47.58, 40.55) * mm, "end": v(-48.98, 39.74) * mm});
            skLineSegment(sketch, "E298", {"start": v(-48.98, 39.74) * mm, "end": v(-48.98, 41.36) * mm});
            skLineSegment(sketch, "E299", {"start": v(-48.98, 41.36) * mm, "end": v(-47.58, 40.55) * mm});
            skLineSegment(sketch, "E300", {"start": v(-52.35, 31.97) * mm, "end": v(-54.03, 32.94) * mm});
            skLineSegment(sketch, "E301", {"start": v(-54.03, 32.94) * mm, "end": v(-52.35, 33.9) * mm});
            skLineSegment(sketch, "E302", {"start": v(-52.35, 33.9) * mm, "end": v(-52.35, 31.97) * mm});
            skLineSegment(sketch, "E303", {"start": v(-53.79, 29.13) * mm, "end": v(-55.77, 27.99) * mm});
            skLineSegment(sketch, "E304", {"start": v(-55.77, 27.99) * mm, "end": v(-55.77, 30.27) * mm});
            skLineSegment(sketch, "E305", {"start": v(-55.77, 30.27) * mm, "end": v(-53.79, 29.13) * mm});
            skLineSegment(sketch, "E306", {"start": v(-58.6, 19.94) * mm, "end": v(-61.32, 21.52) * mm});
            skLineSegment(sketch, "E307", {"start": v(-61.32, 21.52) * mm, "end": v(-58.6, 23.1) * mm});
            skLineSegment(sketch, "E308", {"start": v(-58.6, 23.1) * mm, "end": v(-58.6, 19.94) * mm});
            skLineSegment(sketch, "E309", {"start": v(-59.62, 17.7) * mm, "end": v(-62.74, 15.9) * mm});
            skLineSegment(sketch, "E310", {"start": v(-62.74, 15.9) * mm, "end": v(-62.74, 19.5) * mm});
            skLineSegment(sketch, "E311", {"start": v(-62.74, 19.5) * mm, "end": v(-59.62, 17.7) * mm});
            skLineSegment(sketch, "E312", {"start": v(-64.83, 7.9) * mm, "end": v(-68.62, 10.1) * mm});
            skLineSegment(sketch, "E313", {"start": v(-68.62, 10.1) * mm, "end": v(-64.83, 12.28) * mm});
            skLineSegment(sketch, "E314", {"start": v(-64.83, 12.28) * mm, "end": v(-64.83, 7.9) * mm});
            skLineSegment(sketch, "E315", {"start": v(-65.6, 6.29) * mm, "end": v(-69.65, 3.95) * mm});
            skLineSegment(sketch, "E316", {"start": v(-69.65, 3.95) * mm, "end": v(-69.65, 8.62) * mm});
            skLineSegment(sketch, "E317", {"start": v(-69.65, 8.62) * mm, "end": v(-65.6, 6.29) * mm});
            skLineSegment(sketch, "E318", {"start": v(-65.43, -1.33) * mm, "end": v(-69.73, -3.81) * mm});
            skLineSegment(sketch, "E319", {"start": v(-69.73, -3.81) * mm, "end": v(-69.73, 1.15) * mm});
            skLineSegment(sketch, "E320", {"start": v(-69.73, 1.15) * mm, "end": v(-65.43, -1.33) * mm});
            skLineSegment(sketch, "E321", {"start": v(-64.66, -7.64) * mm, "end": v(-68.98, -5.14) * mm});
            skLineSegment(sketch, "E322", {"start": v(-68.98, -5.14) * mm, "end": v(-64.66, -2.64) * mm});
            skLineSegment(sketch, "E323", {"start": v(-64.66, -2.64) * mm, "end": v(-64.66, -7.64) * mm});
            skLineSegment(sketch, "E324", {"start": v(-58.8, -12.75) * mm, "end": v(-63.16, -15.27) * mm});
            skLineSegment(sketch, "E325", {"start": v(-63.16, -15.27) * mm, "end": v(-63.16, -10.23) * mm});
            skLineSegment(sketch, "E326", {"start": v(-63.16, -10.23) * mm, "end": v(-58.8, -12.75) * mm});
            skLineSegment(sketch, "E327", {"start": v(-58.05, -19.07) * mm, "end": v(-62.4, -16.56) * mm});
            skLineSegment(sketch, "E328", {"start": v(-62.4, -16.56) * mm, "end": v(-58.05, -14.05) * mm});
            skLineSegment(sketch, "E329", {"start": v(-58.05, -14.05) * mm, "end": v(-58.05, -19.07) * mm});
            skLineSegment(sketch, "E330", {"start": v(-52.28, -24.17) * mm, "end": v(-56.52, -26.62) * mm});
            skLineSegment(sketch, "E331", {"start": v(-56.52, -26.62) * mm, "end": v(-56.52, -21.73) * mm});
            skLineSegment(sketch, "E332", {"start": v(-56.52, -21.73) * mm, "end": v(-52.28, -24.17) * mm});
            skLineSegment(sketch, "E333", {"start": v(-51.54, -30.35) * mm, "end": v(-55.65, -27.98) * mm});
            skLineSegment(sketch, "E334", {"start": v(-55.65, -27.98) * mm, "end": v(-51.54, -25.61) * mm});
            skLineSegment(sketch, "E335", {"start": v(-51.54, -25.61) * mm, "end": v(-51.54, -30.35) * mm});
            skLineSegment(sketch, "E336", {"start": v(-45.94, -35.6) * mm, "end": v(-49.8, -37.83) * mm});
            skLineSegment(sketch, "E337", {"start": v(-49.8, -37.83) * mm, "end": v(-49.8, -33.36) * mm});
            skLineSegment(sketch, "E338", {"start": v(-49.8, -33.36) * mm, "end": v(-45.94, -35.6) * mm});
            skLineSegment(sketch, "E339", {"start": v(-45.02, -41.65) * mm, "end": v(-48.9, -39.4) * mm});
            skLineSegment(sketch, "E340", {"start": v(-48.9, -39.4) * mm, "end": v(-45.02, -37.16) * mm});
            skLineSegment(sketch, "E341", {"start": v(-45.02, -37.16) * mm, "end": v(-45.02, -41.65) * mm});
            skLineSegment(sketch, "E342", {"start": v(-44.98, -49.33) * mm, "end": v(-48.98, -47.02) * mm});
            skLineSegment(sketch, "E343", {"start": v(-48.98, -47.02) * mm, "end": v(-44.98, -44.71) * mm});
            skLineSegment(sketch, "E344", {"start": v(-44.98, -44.71) * mm, "end": v(-44.98, -49.33) * mm});
            skLineSegment(sketch, "E345", {"start": v(-39.2, -47.02) * mm, "end": v(-43.27, -49.37) * mm});
            skLineSegment(sketch, "E346", {"start": v(-43.27, -49.37) * mm, "end": v(-43.27, -44.67) * mm});
            skLineSegment(sketch, "E347", {"start": v(-43.27, -44.67) * mm, "end": v(-39.2, -47.02) * mm});
            skLineSegment(sketch, "E348", {"start": v(-31.71, -49.46) * mm, "end": v(-35.95, -47.02) * mm});
            skLineSegment(sketch, "E349", {"start": v(-35.95, -47.02) * mm, "end": v(-31.71, -44.57) * mm});
            skLineSegment(sketch, "E350", {"start": v(-31.71, -44.57) * mm, "end": v(-31.71, -49.46) * mm});
            skLineSegment(sketch, "E351", {"start": v(-25.87, -47.02) * mm, "end": v(-30.16, -49.5) * mm});
            skLineSegment(sketch, "E352", {"start": v(-30.16, -49.5) * mm, "end": v(-30.16, -44.54) * mm});
            skLineSegment(sketch, "E353", {"start": v(-30.16, -44.54) * mm, "end": v(-25.87, -47.02) * mm});
            skLineSegment(sketch, "E354", {"start": v(-18.53, -49.45) * mm, "end": v(-22.75, -47.02) * mm});
            skLineSegment(sketch, "E355", {"start": v(-22.75, -47.02) * mm, "end": v(-18.53, -44.58) * mm});
            skLineSegment(sketch, "E356", {"start": v(-18.53, -44.58) * mm, "end": v(-18.53, -49.45) * mm});
            skLineSegment(sketch, "E357", {"start": v(-41.02, 51.97) * mm, "end": v(-42.36, 51.2) * mm});
            skLineSegment(sketch, "E358", {"start": v(-42.36, 51.2) * mm, "end": v(-42.36, 52.75) * mm});
            skLineSegment(sketch, "E359", {"start": v(-42.36, 52.75) * mm, "end": v(-41.02, 51.97) * mm});
            skLineSegment(sketch, "E360", {"start": v(-45.68, 50.88) * mm, "end": v(-47.58, 51.97) * mm});
            skLineSegment(sketch, "E361", {"start": v(-47.58, 51.97) * mm, "end": v(-45.68, 53.07) * mm});
            skLineSegment(sketch, "E362", {"start": v(-45.68, 53.07) * mm, "end": v(-45.68, 50.88) * mm});
            skLineSegment(sketch, "E363", {"start": v(-47.22, 48.17) * mm, "end": v(-49.16, 47.05) * mm});
            skLineSegment(sketch, "E364", {"start": v(-49.16, 47.05) * mm, "end": v(-49.16, 49.29) * mm});
            skLineSegment(sketch, "E365", {"start": v(-49.16, 49.29) * mm, "end": v(-47.22, 48.17) * mm});
            skLineSegment(sketch, "E366", {"start": v(-52.23, 39.37) * mm, "end": v(-54.27, 40.55) * mm});
            skLineSegment(sketch, "E367", {"start": v(-54.27, 40.55) * mm, "end": v(-52.23, 41.73) * mm});
            skLineSegment(sketch, "E368", {"start": v(-52.23, 41.73) * mm, "end": v(-52.23, 39.37) * mm});
            skLineSegment(sketch, "E369", {"start": v(-53.64, 36.74) * mm, "end": v(-55.84, 35.48) * mm});
            skLineSegment(sketch, "E370", {"start": v(-55.84, 35.48) * mm, "end": v(-55.84, 38.01) * mm});
            skLineSegment(sketch, "E371", {"start": v(-55.84, 38.01) * mm, "end": v(-53.64, 36.74) * mm});
            skLineSegment(sketch, "E372", {"start": v(-58.6, 27.55) * mm, "end": v(-61.32, 29.13) * mm});
            skLineSegment(sketch, "E373", {"start": v(-61.32, 29.13) * mm, "end": v(-58.6, 30.7) * mm});
            skLineSegment(sketch, "E374", {"start": v(-58.6, 30.7) * mm, "end": v(-58.6, 27.55) * mm});
            skLineSegment(sketch, "E375", {"start": v(-59.68, 25.32) * mm, "end": v(-62.71, 23.57) * mm});
            skLineSegment(sketch, "E376", {"start": v(-62.71, 23.57) * mm, "end": v(-62.71, 27.07) * mm});
            skLineSegment(sketch, "E377", {"start": v(-62.71, 27.07) * mm, "end": v(-59.68, 25.32) * mm});
            skLineSegment(sketch, "E378", {"start": v(-64.9, 15.62) * mm, "end": v(-68.5, 17.7) * mm});
            skLineSegment(sketch, "E379", {"start": v(-68.5, 17.7) * mm, "end": v(-64.9, 19.8) * mm});
            skLineSegment(sketch, "E380", {"start": v(-64.9, 19.8) * mm, "end": v(-64.9, 15.62) * mm});
            skLineSegment(sketch, "E381", {"start": v(-65.73, 13.9) * mm, "end": v(-69.58, 11.68) * mm});
            skLineSegment(sketch, "E382", {"start": v(-69.58, 11.68) * mm, "end": v(-69.58, 16.12) * mm});
            skLineSegment(sketch, "E383", {"start": v(-69.58, 16.12) * mm, "end": v(-65.73, 13.9) * mm});
            skLineSegment(sketch, "E384", {"start": v(-65.3, -8.94) * mm, "end": v(-69.8, -11.54) * mm});
            skLineSegment(sketch, "E385", {"start": v(-69.8, -11.54) * mm, "end": v(-69.8, -6.35) * mm});
            skLineSegment(sketch, "E386", {"start": v(-69.8, -6.35) * mm, "end": v(-65.3, -8.94) * mm});
            skLineSegment(sketch, "E387", {"start": v(-64.6, -15.34) * mm, "end": v(-69.1, -12.75) * mm});
            skLineSegment(sketch, "E388", {"start": v(-69.1, -12.75) * mm, "end": v(-64.6, -10.16) * mm});
            skLineSegment(sketch, "E389", {"start": v(-64.6, -10.16) * mm, "end": v(-64.6, -15.34) * mm});
            skLineSegment(sketch, "E390", {"start": v(-58.8, -20.37) * mm, "end": v(-63.15, -22.87) * mm});
            skLineSegment(sketch, "E391", {"start": v(-63.15, -22.87) * mm, "end": v(-63.15, -17.86) * mm});
            skLineSegment(sketch, "E392", {"start": v(-63.15, -17.86) * mm, "end": v(-58.8, -20.37) * mm});
            skLineSegment(sketch, "E393", {"start": v(-58.1, -26.6) * mm, "end": v(-62.3, -24.17) * mm});
            skLineSegment(sketch, "E394", {"start": v(-62.3, -24.17) * mm, "end": v(-58.1, -21.76) * mm});
            skLineSegment(sketch, "E395", {"start": v(-58.1, -21.76) * mm, "end": v(-58.1, -26.6) * mm});
            skLineSegment(sketch, "E396", {"start": v(-52.53, -31.79) * mm, "end": v(-56.4, -34.02) * mm});
            skLineSegment(sketch, "E397", {"start": v(-56.4, -34.02) * mm, "end": v(-56.4, -29.56) * mm});
            skLineSegment(sketch, "E398", {"start": v(-56.4, -29.56) * mm, "end": v(-52.53, -31.79) * mm});
            skLineSegment(sketch, "E399", {"start": v(-51.64, -37.8) * mm, "end": v(-55.44, -35.6) * mm});
            skLineSegment(sketch, "E400", {"start": v(-55.44, -35.6) * mm, "end": v(-51.64, -33.4) * mm});
            skLineSegment(sketch, "E401", {"start": v(-51.64, -33.4) * mm, "end": v(-51.64, -37.8) * mm});
            skLineSegment(sketch, "E402", {"start": v(-45.9, -43.21) * mm, "end": v(-49.82, -45.47) * mm});
            skLineSegment(sketch, "E403", {"start": v(-49.82, -45.47) * mm, "end": v(-49.82, -40.95) * mm});
            skLineSegment(sketch, "E404", {"start": v(-49.82, -40.95) * mm, "end": v(-45.9, -43.21) * mm});
            skLineSegment(sketch, "E405", {"start": v(-52.06, 46.7) * mm, "end": v(-54.6, 48.17) * mm});
            skLineSegment(sketch, "E406", {"start": v(-54.6, 48.17) * mm, "end": v(-52.06, 49.63) * mm});
            skLineSegment(sketch, "E407", {"start": v(-52.06, 49.63) * mm, "end": v(-52.06, 46.7) * mm});
            skLineSegment(sketch, "E408", {"start": v(-53.36, 44.36) * mm, "end": v(-55.98, 42.85) * mm});
            skLineSegment(sketch, "E409", {"start": v(-55.98, 42.85) * mm, "end": v(-55.98, 45.87) * mm});
            skLineSegment(sketch, "E410", {"start": v(-55.98, 45.87) * mm, "end": v(-53.36, 44.36) * mm});
            skLineSegment(sketch, "E411", {"start": v(-58.54, 35.07) * mm, "end": v(-61.44, 36.74) * mm});
            skLineSegment(sketch, "E412", {"start": v(-61.44, 36.74) * mm, "end": v(-58.54, 38.42) * mm});
            skLineSegment(sketch, "E413", {"start": v(-58.54, 38.42) * mm, "end": v(-58.54, 35.07) * mm});
            skLineSegment(sketch, "E414", {"start": v(-59.63, 32.94) * mm, "end": v(-62.74, 31.14) * mm});
            skLineSegment(sketch, "E415", {"start": v(-62.74, 31.14) * mm, "end": v(-62.74, 34.73) * mm});
            skLineSegment(sketch, "E416", {"start": v(-62.74, 34.73) * mm, "end": v(-59.63, 32.94) * mm});
            skLineSegment(sketch, "E417", {"start": v(-64.92, 23.28) * mm, "end": v(-68.46, 25.32) * mm});
            skLineSegment(sketch, "E418", {"start": v(-68.46, 25.32) * mm, "end": v(-64.92, 27.37) * mm});
            skLineSegment(sketch, "E419", {"start": v(-64.92, 27.37) * mm, "end": v(-64.92, 23.28) * mm});
            skLineSegment(sketch, "E420", {"start": v(-65.81, 21.52) * mm, "end": v(-69.54, 19.36) * mm});
            skLineSegment(sketch, "E421", {"start": v(-69.54, 19.36) * mm, "end": v(-69.54, 23.67) * mm});
            skLineSegment(sketch, "E422", {"start": v(-69.54, 23.67) * mm, "end": v(-65.81, 21.52) * mm});
            skLineSegment(sketch, "E423", {"start": v(-65.33, -16.56) * mm, "end": v(-69.78, -19.13) * mm});
            skLineSegment(sketch, "E424", {"start": v(-69.78, -19.13) * mm, "end": v(-69.78, -13.99) * mm});
            skLineSegment(sketch, "E425", {"start": v(-69.78, -13.99) * mm, "end": v(-65.33, -16.56) * mm});
            skLineSegment(sketch, "E426", {"start": v(-64.67, -22.84) * mm, "end": v(-68.96, -20.37) * mm});
            skLineSegment(sketch, "E427", {"start": v(-68.96, -20.37) * mm, "end": v(-64.67, -17.9) * mm});
            skLineSegment(sketch, "E428", {"start": v(-64.67, -17.9) * mm, "end": v(-64.67, -22.84) * mm});
            skLineSegment(sketch, "E429", {"start": v(-59.13, -27.98) * mm, "end": v(-62.99, -30.21) * mm});
            skLineSegment(sketch, "E430", {"start": v(-62.99, -30.21) * mm, "end": v(-62.99, -25.75) * mm});
            skLineSegment(sketch, "E431", {"start": v(-62.99, -25.75) * mm, "end": v(-59.13, -27.98) * mm});
            skLineSegment(sketch, "E432", {"start": v(-58.27, -33.93) * mm, "end": v(-61.98, -31.79) * mm});
            skLineSegment(sketch, "E433", {"start": v(-61.98, -31.79) * mm, "end": v(-58.27, -29.64) * mm});
            skLineSegment(sketch, "E434", {"start": v(-58.27, -29.64) * mm, "end": v(-58.27, -33.93) * mm});
            skLineSegment(sketch, "E435", {"start": v(-52.61, -39.4) * mm, "end": v(-56.36, -41.57) * mm});
            skLineSegment(sketch, "E436", {"start": v(-56.36, -41.57) * mm, "end": v(-56.36, -37.24) * mm});
            skLineSegment(sketch, "E437", {"start": v(-56.36, -37.24) * mm, "end": v(-52.61, -39.4) * mm});
            skLineSegment(sketch, "E438", {"start": v(-51.63, -45.43) * mm, "end": v(-55.47, -43.21) * mm});
            skLineSegment(sketch, "E439", {"start": v(-55.47, -43.21) * mm, "end": v(-51.63, -41) * mm});
            skLineSegment(sketch, "E440", {"start": v(-51.63, -41) * mm, "end": v(-51.63, -45.43) * mm});
            skLineSegment(sketch, "E441", {"start": v(-53.1, 51.97) * mm, "end": v(-56.1, 50.24) * mm});
            skLineSegment(sketch, "E442", {"start": v(-56.1, 50.24) * mm, "end": v(-56.1, 53.71) * mm});
            skLineSegment(sketch, "E443", {"start": v(-56.1, 53.71) * mm, "end": v(-53.1, 51.97) * mm});
            skLineSegment(sketch, "E444", {"start": v(-58.45, 42.53) * mm, "end": v(-61.62, 44.36) * mm});
            skLineSegment(sketch, "E445", {"start": v(-61.62, 44.36) * mm, "end": v(-58.45, 46.2) * mm});
            skLineSegment(sketch, "E446", {"start": v(-58.45, 46.2) * mm, "end": v(-58.45, 42.53) * mm});
            skLineSegment(sketch, "E447", {"start": v(-59.51, 40.55) * mm, "end": v(-62.8, 38.66) * mm});
            skLineSegment(sketch, "E448", {"start": v(-62.8, 38.66) * mm, "end": v(-62.8, 42.45) * mm});
            skLineSegment(sketch, "E449", {"start": v(-62.8, 42.45) * mm, "end": v(-59.51, 40.55) * mm});
            skLineSegment(sketch, "E450", {"start": v(-64.9, 30.87) * mm, "end": v(-68.48, 32.94) * mm});
            skLineSegment(sketch, "E451", {"start": v(-68.48, 32.94) * mm, "end": v(-64.9, 35) * mm});
            skLineSegment(sketch, "E452", {"start": v(-64.9, 35) * mm, "end": v(-64.9, 30.87) * mm});
            skLineSegment(sketch, "E453", {"start": v(-65.82, 29.13) * mm, "end": v(-69.54, 26.98) * mm});
            skLineSegment(sketch, "E454", {"start": v(-69.54, 26.98) * mm, "end": v(-69.54, 31.28) * mm});
            skLineSegment(sketch, "E455", {"start": v(-69.54, 31.28) * mm, "end": v(-65.82, 29.13) * mm});
            skLineSegment(sketch, "E456", {"start": v(-65.68, -24.17) * mm, "end": v(-69.6, -26.44) * mm});
            skLineSegment(sketch, "E457", {"start": v(-69.6, -26.44) * mm, "end": v(-69.6, -21.9) * mm});
            skLineSegment(sketch, "E458", {"start": v(-69.6, -21.9) * mm, "end": v(-65.68, -24.17) * mm});
            skLineSegment(sketch, "E459", {"start": v(-64.87, -30.1) * mm, "end": v(-68.55, -27.98) * mm});
            skLineSegment(sketch, "E460", {"start": v(-68.55, -27.98) * mm, "end": v(-64.87, -25.85) * mm});
            skLineSegment(sketch, "E461", {"start": v(-64.87, -25.85) * mm, "end": v(-64.87, -30.1) * mm});
            skLineSegment(sketch, "E462", {"start": v(-59.31, -35.6) * mm, "end": v(-62.9, -37.66) * mm});
            skLineSegment(sketch, "E463", {"start": v(-62.9, -37.66) * mm, "end": v(-62.9, -33.53) * mm});
            skLineSegment(sketch, "E464", {"start": v(-62.9, -33.53) * mm, "end": v(-59.31, -35.6) * mm});
            skLineSegment(sketch, "E465", {"start": v(-58.28, -41.52) * mm, "end": v(-61.94, -39.4) * mm});
            skLineSegment(sketch, "E466", {"start": v(-61.94, -39.4) * mm, "end": v(-58.28, -37.29) * mm});
            skLineSegment(sketch, "E467", {"start": v(-58.28, -37.29) * mm, "end": v(-58.28, -41.52) * mm});
            skLineSegment(sketch, "E468", {"start": v(-52.55, -47.02) * mm, "end": v(-56.39, -49.24) * mm});
            skLineSegment(sketch, "E469", {"start": v(-56.39, -49.24) * mm, "end": v(-56.39, -44.8) * mm});
            skLineSegment(sketch, "E470", {"start": v(-56.39, -44.8) * mm, "end": v(-52.55, -47.02) * mm});
            skLineSegment(sketch, "E471", {"start": v(-58.37, 50.01) * mm, "end": v(-61.77, 51.97) * mm});
            skLineSegment(sketch, "E472", {"start": v(-61.77, 51.97) * mm, "end": v(-58.37, 53.93) * mm});
            skLineSegment(sketch, "E473", {"start": v(-58.37, 53.93) * mm, "end": v(-58.37, 50.01) * mm});
            skLineSegment(sketch, "E474", {"start": v(-59.39, 48.17) * mm, "end": v(-62.86, 46.16) * mm});
            skLineSegment(sketch, "E475", {"start": v(-62.86, 46.16) * mm, "end": v(-62.86, 50.17) * mm});
            skLineSegment(sketch, "E476", {"start": v(-62.86, 50.17) * mm, "end": v(-59.39, 48.17) * mm});
            skLineSegment(sketch, "E477", {"start": v(-64.88, 38.44) * mm, "end": v(-68.54, 40.55) * mm});
            skLineSegment(sketch, "E478", {"start": v(-68.54, 40.55) * mm, "end": v(-64.88, 42.66) * mm});
            skLineSegment(sketch, "E479", {"start": v(-64.88, 42.66) * mm, "end": v(-64.88, 38.44) * mm});
            skLineSegment(sketch, "E480", {"start": v(-65.79, 36.74) * mm, "end": v(-69.55, 34.57) * mm});
            skLineSegment(sketch, "E481", {"start": v(-69.55, 34.57) * mm, "end": v(-69.55, 38.92) * mm});
            skLineSegment(sketch, "E482", {"start": v(-69.55, 38.92) * mm, "end": v(-65.79, 36.74) * mm});
            skLineSegment(sketch, "E483", {"start": v(-66, -31.79) * mm, "end": v(-69.45, -33.78) * mm});
            skLineSegment(sketch, "E484", {"start": v(-69.45, -33.78) * mm, "end": v(-69.45, -29.8) * mm});
            skLineSegment(sketch, "E485", {"start": v(-69.45, -29.8) * mm, "end": v(-66, -31.79) * mm});
            skLineSegment(sketch, "E486", {"start": v(-64.94, -37.6) * mm, "end": v(-68.42, -35.6) * mm});
            skLineSegment(sketch, "E487", {"start": v(-68.42, -35.6) * mm, "end": v(-64.94, -33.59) * mm});
            skLineSegment(sketch, "E488", {"start": v(-64.94, -33.59) * mm, "end": v(-64.94, -37.6) * mm});
            skLineSegment(sketch, "E489", {"start": v(-59.24, -43.21) * mm, "end": v(-62.93, -45.34) * mm});
            skLineSegment(sketch, "E490", {"start": v(-62.93, -45.34) * mm, "end": v(-62.93, -41.08) * mm});
            skLineSegment(sketch, "E491", {"start": v(-62.93, -41.08) * mm, "end": v(-59.24, -43.21) * mm});
            skLineSegment(sketch, "E492", {"start": v(-58.25, -49.2) * mm, "end": v(-62.02, -47.02) * mm});
            skLineSegment(sketch, "E493", {"start": v(-62.02, -47.02) * mm, "end": v(-58.25, -44.84) * mm});
            skLineSegment(sketch, "E494", {"start": v(-58.25, -44.84) * mm, "end": v(-58.25, -49.2) * mm});
            skLineSegment(sketch, "E495", {"start": v(-64.86, 46.03) * mm, "end": v(-68.57, 48.17) * mm});
            skLineSegment(sketch, "E496", {"start": v(-68.57, 48.17) * mm, "end": v(-64.86, 50.3) * mm});
            skLineSegment(sketch, "E497", {"start": v(-64.86, 50.3) * mm, "end": v(-64.86, 46.03) * mm});
            skLineSegment(sketch, "E498", {"start": v(-65.77, 44.36) * mm, "end": v(-69.56, 42.17) * mm});
            skLineSegment(sketch, "E499", {"start": v(-69.56, 42.17) * mm, "end": v(-69.56, 46.55) * mm});
            skLineSegment(sketch, "E500", {"start": v(-69.56, 46.55) * mm, "end": v(-65.77, 44.36) * mm});
            skLineSegment(sketch, "E501", {"start": v(-65.95, -39.4) * mm, "end": v(-69.47, -41.44) * mm});
            skLineSegment(sketch, "E502", {"start": v(-69.47, -41.44) * mm, "end": v(-69.47, -37.37) * mm});
            skLineSegment(sketch, "E503", {"start": v(-69.47, -37.37) * mm, "end": v(-65.95, -39.4) * mm});
            skLineSegment(sketch, "E504", {"start": v(-64.89, -45.31) * mm, "end": v(-68.52, -43.21) * mm});
            skLineSegment(sketch, "E505", {"start": v(-68.52, -43.21) * mm, "end": v(-64.89, -41.11) * mm});
            skLineSegment(sketch, "E506", {"start": v(-64.89, -41.11) * mm, "end": v(-64.89, -45.31) * mm});
            skLineSegment(sketch, "E507", {"start": v(-65.78, 51.97) * mm, "end": v(-69.55, 49.8) * mm});
            skLineSegment(sketch, "E508", {"start": v(-69.55, 49.8) * mm, "end": v(-69.55, 54.15) * mm});
            skLineSegment(sketch, "E509", {"start": v(-69.55, 54.15) * mm, "end": v(-65.78, 51.97) * mm});
            skLineSegment(sketch, "E510", {"start": v(-65.87, -47.02) * mm, "end": v(-69.51, -49.12) * mm});
            skLineSegment(sketch, "E511", {"start": v(-69.51, -49.12) * mm, "end": v(-69.51, -44.91) * mm});
            skLineSegment(sketch, "E512", {"start": v(-69.51, -44.91) * mm, "end": v(-65.87, -47.02) * mm});
            skPoint(sketch, "E513", {"position": v(-69.8, -41.84) * mm});
            skSolve(sketch);
        }
        {
            var Q0;
            Q0=makeQuery(id+"F6.imprint","IMPRINT",FACE,{"disambiguationData":[TD([[makeQuery(id+"F6.imprint","IMPRINT",EDGE,{"derivedFrom":sQuery(id+"F6.wireOp",EDGE,"E396")}),-1.0]])]});
            var Q1;
            Q1=makeQuery(id+"F6.imprint","IMPRINT",FACE,{"disambiguationData":[TD([[makeQuery(id+"F6.imprint","IMPRINT",EDGE,{"derivedFrom":sQuery(id+"F6.wireOp",EDGE,"E420")}),-1.0]])]});
            var Q2;
            Q2=makeQuery(id+"F6.imprint","IMPRINT",FACE,{"disambiguationData":[TD([[makeQuery(id+"F6.imprint","IMPRINT",EDGE,{"derivedFrom":sQuery(id+"F6.wireOp",EDGE,"E120")}),-1.0]])]});
            var Q3;
            Q3=makeQuery(id+"F6.imprint","IMPRINT",FACE,{"disambiguationData":[TD([[makeQuery(id+"F6.imprint","IMPRINT",EDGE,{"derivedFrom":sQuery(id+"F6.wireOp",EDGE,"E12")}),-1.0]])]});
            var Q4;
            Q4=makeQuery(id+"F6.imprint","IMPRINT",FACE,{"disambiguationData":[TD([[makeQuery(id+"F6.imprint","IMPRINT",EDGE,{"derivedFrom":sQuery(id+"F6.wireOp",EDGE,"E168")}),-1.0]])]});
            var Q5;
            Q5=makeQuery(id+"F6.imprint","IMPRINT",FACE,{"disambiguationData":[TD([[makeQuery(id+"F6.imprint","IMPRINT",EDGE,{"derivedFrom":sQuery(id+"F6.wireOp",EDGE,"E456")}),-1.0]])]});
            var Q6;
            Q6=makeQuery(id+"F6.imprint","IMPRINT",FACE,{"disambiguationData":[TD([[makeQuery(id+"F6.imprint","IMPRINT",EDGE,{"derivedFrom":sQuery(id+"F6.wireOp",EDGE,"E15")}),-1.0]])]});
            var Q7;
            Q7=makeQuery(id+"F6.imprint","IMPRINT",FACE,{"disambiguationData":[TD([[makeQuery(id+"F6.imprint","IMPRINT",EDGE,{"derivedFrom":sQuery(id+"F6.wireOp",EDGE,"E231")}),-1.0]])]});
            var Q8;
            Q8=makeQuery(id+"F6.imprint","IMPRINT",FACE,{"disambiguationData":[TD([[makeQuery(id+"F6.imprint","IMPRINT",EDGE,{"derivedFrom":sQuery(id+"F6.wireOp",EDGE,"E417")}),-1.0]])]});
            var Q9;
            Q9=makeQuery(id+"F6.imprint","IMPRINT",FACE,{"disambiguationData":[TD([[makeQuery(id+"F6.imprint","IMPRINT",EDGE,{"derivedFrom":sQuery(id+"F6.wireOp",EDGE,"E150")}),-1.0]])]});
            var Q10;
            Q10=makeQuery(id+"F6.imprint","IMPRINT",FACE,{"disambiguationData":[TD([[makeQuery(id+"F6.imprint","IMPRINT",EDGE,{"derivedFrom":sQuery(id+"F6.wireOp",EDGE,"E24")}),-1.0]])]});
            var Q11;
            Q11=makeQuery(id+"F6.imprint","IMPRINT",FACE,{"disambiguationData":[TD([[makeQuery(id+"F6.imprint","IMPRINT",EDGE,{"derivedFrom":sQuery(id+"F6.wireOp",EDGE,"E165")}),-1.0]])]});
            var Q12;
            Q12=makeQuery(id+"F6.imprint","IMPRINT",FACE,{"disambiguationData":[TD([[makeQuery(id+"F6.imprint","IMPRINT",EDGE,{"derivedFrom":sQuery(id+"F6.wireOp",EDGE,"E93")}),-1.0]])]});
            var Q13;
            Q13=makeQuery(id+"F6.imprint","IMPRINT",FACE,{"disambiguationData":[TD([[makeQuery(id+"F6.imprint","IMPRINT",EDGE,{"derivedFrom":sQuery(id+"F6.wireOp",EDGE,"E3")}),-1.0]])]});
            var Q14;
            Q14=makeQuery(id+"F6.imprint","IMPRINT",FACE,{"disambiguationData":[TD([[makeQuery(id+"F6.imprint","IMPRINT",EDGE,{"derivedFrom":sQuery(id+"F6.wireOp",EDGE,"E390")}),-1.0]])]});
            var Q15;
            Q15=makeQuery(id+"F6.imprint","IMPRINT",FACE,{"disambiguationData":[TD([[makeQuery(id+"F6.imprint","IMPRINT",EDGE,{"derivedFrom":sQuery(id+"F6.wireOp",EDGE,"E114")}),-1.0]])]});
            var Q16;
            Q16=makeQuery(id+"F6.imprint","IMPRINT",FACE,{"disambiguationData":[TD([[makeQuery(id+"F6.imprint","IMPRINT",EDGE,{"derivedFrom":sQuery(id+"F6.wireOp",EDGE,"E75")}),-1.0]])]});
            var Q17;
            Q17=makeQuery(id+"F6.imprint","IMPRINT",FACE,{"disambiguationData":[TD([[makeQuery(id+"F6.imprint","IMPRINT",EDGE,{"derivedFrom":sQuery(id+"F6.wireOp",EDGE,"E207")}),-1.0]])]});
            var Q18;
            Q18=makeQuery(id+"F6.imprint","IMPRINT",FACE,{"disambiguationData":[TD([[makeQuery(id+"F6.imprint","IMPRINT",EDGE,{"derivedFrom":sQuery(id+"F6.wireOp",EDGE,"E57")}),-1.0]])]});
            var Q19;
            Q19=makeQuery(id+"F6.imprint","IMPRINT",FACE,{"disambiguationData":[TD([[makeQuery(id+"F6.imprint","IMPRINT",EDGE,{"derivedFrom":sQuery(id+"F6.wireOp",EDGE,"E33")}),-1.0]])]});
            var Q20;
            Q20=makeQuery(id+"F6.imprint","IMPRINT",FACE,{"disambiguationData":[TD([[makeQuery(id+"F6.imprint","IMPRINT",EDGE,{"derivedFrom":sQuery(id+"F6.wireOp",EDGE,"E90")}),-1.0]])]});
            var Q21;
            Q21=makeQuery(id+"F6.imprint","IMPRINT",FACE,{"disambiguationData":[TD([[makeQuery(id+"F6.imprint","IMPRINT",EDGE,{"derivedFrom":sQuery(id+"F6.wireOp",EDGE,"E141")}),-1.0]])]});
            var Q22;
            Q22=makeQuery(id+"F6.imprint","IMPRINT",FACE,{"disambiguationData":[TD([[makeQuery(id+"F6.imprint","IMPRINT",EDGE,{"derivedFrom":sQuery(id+"F6.wireOp",EDGE,"E126")}),-1.0]])]});
            var Q23;
            Q23=makeQuery(id+"F6.imprint","IMPRINT",FACE,{"disambiguationData":[TD([[makeQuery(id+"F6.imprint","IMPRINT",EDGE,{"derivedFrom":sQuery(id+"F6.wireOp",EDGE,"E111")}),-1.0]])]});
            var Q24;
            Q24=makeQuery(id+"F6.imprint","IMPRINT",FACE,{"disambiguationData":[TD([[makeQuery(id+"F6.imprint","IMPRINT",EDGE,{"derivedFrom":sQuery(id+"F6.wireOp",EDGE,"E375")}),-1.0]])]});
            var Q25;
            Q25=makeQuery(id+"F6.imprint","IMPRINT",FACE,{"disambiguationData":[TD([[makeQuery(id+"F6.imprint","IMPRINT",EDGE,{"derivedFrom":sQuery(id+"F6.wireOp",EDGE,"E249")}),-1.0]])]});
            var Q26;
            Q26=makeQuery(id+"F6.imprint","IMPRINT",FACE,{"disambiguationData":[TD([[makeQuery(id+"F6.imprint","IMPRINT",EDGE,{"derivedFrom":sQuery(id+"F6.wireOp",EDGE,"E426")}),-1.0]])]});
            var Q27;
            Q27=makeQuery(id+"F6.imprint","IMPRINT",FACE,{"disambiguationData":[TD([[makeQuery(id+"F6.imprint","IMPRINT",EDGE,{"derivedFrom":sQuery(id+"F6.wireOp",EDGE,"E330")}),-1.0]])]});
            var Q28;
            Q28=makeQuery(id+"F6.imprint","IMPRINT",FACE,{"disambiguationData":[TD([[makeQuery(id+"F6.imprint","IMPRINT",EDGE,{"derivedFrom":sQuery(id+"F6.wireOp",EDGE,"E138")}),-1.0]])]});
            var Q29;
            Q29=makeQuery(id+"F6.imprint","IMPRINT",FACE,{"disambiguationData":[TD([[makeQuery(id+"F6.imprint","IMPRINT",EDGE,{"derivedFrom":sQuery(id+"F6.wireOp",EDGE,"E177")}),-1.0]])]});
            var Q30;
            Q30=makeQuery(id+"F6.imprint","IMPRINT",FACE,{"disambiguationData":[TD([[makeQuery(id+"F6.imprint","IMPRINT",EDGE,{"derivedFrom":sQuery(id+"F6.wireOp",EDGE,"E54")}),-1.0]])]});
            var Q31;
            Q31=makeQuery(id+"F6.imprint","IMPRINT",FACE,{"disambiguationData":[TD([[makeQuery(id+"F6.imprint","IMPRINT",EDGE,{"derivedFrom":sQuery(id+"F6.wireOp",EDGE,"E384")}),-1.0]])]});
            var Q32;
            Q32=makeQuery(id+"F6.imprint","IMPRINT",FACE,{"disambiguationData":[TD([[makeQuery(id+"F6.imprint","IMPRINT",EDGE,{"derivedFrom":sQuery(id+"F6.wireOp",EDGE,"E45")}),-1.0]])]});
            var Q33;
            Q33=makeQuery(id+"F6.imprint","IMPRINT",FACE,{"disambiguationData":[TD([[makeQuery(id+"F6.imprint","IMPRINT",EDGE,{"derivedFrom":sQuery(id+"F6.wireOp",EDGE,"E336")}),-1.0]])]});
            var Q34;
            Q34=makeQuery(id+"F6.imprint","IMPRINT",FACE,{"disambiguationData":[TD([[makeQuery(id+"F6.imprint","IMPRINT",EDGE,{"derivedFrom":sQuery(id+"F6.wireOp",EDGE,"E36")}),-1.0]])]});
            var Q35;
            Q35=makeQuery(id+"F6.imprint","IMPRINT",FACE,{"disambiguationData":[TD([[makeQuery(id+"F6.imprint","IMPRINT",EDGE,{"derivedFrom":sQuery(id+"F6.wireOp",EDGE,"E213")}),-1.0]])]});
            var Q36;
            Q36=makeQuery(id+"F6.imprint","IMPRINT",FACE,{"disambiguationData":[TD([[makeQuery(id+"F6.imprint","IMPRINT",EDGE,{"derivedFrom":sQuery(id+"F6.wireOp",EDGE,"E315")}),-1.0]])]});
            var Q37;
            Q37=makeQuery(id+"F6.imprint","IMPRINT",FACE,{"disambiguationData":[TD([[makeQuery(id+"F6.imprint","IMPRINT",EDGE,{"derivedFrom":sQuery(id+"F6.wireOp",EDGE,"E162")}),-1.0]])]});
            var Q38;
            Q38=makeQuery(id+"F6.imprint","IMPRINT",FACE,{"disambiguationData":[TD([[makeQuery(id+"F6.imprint","IMPRINT",EDGE,{"derivedFrom":sQuery(id+"F6.wireOp",EDGE,"E300")}),-1.0]])]});
            var Q39;
            Q39=makeQuery(id+"F6.imprint","IMPRINT",FACE,{"disambiguationData":[TD([[makeQuery(id+"F6.imprint","IMPRINT",EDGE,{"derivedFrom":sQuery(id+"F6.wireOp",EDGE,"E267")}),-1.0]])]});
            var Q40;
            Q40=makeQuery(id+"F6.imprint","IMPRINT",FACE,{"disambiguationData":[TD([[makeQuery(id+"F6.imprint","IMPRINT",EDGE,{"derivedFrom":sQuery(id+"F6.wireOp",EDGE,"E18")}),-1.0]])]});
            var Q41;
            Q41=makeQuery(id+"F6.imprint","IMPRINT",FACE,{"disambiguationData":[TD([[makeQuery(id+"F6.imprint","IMPRINT",EDGE,{"derivedFrom":sQuery(id+"F6.wireOp",EDGE,"E378")}),-1.0]])]});
            var Q42;
            Q42=makeQuery(id+"F6.imprint","IMPRINT",FACE,{"disambiguationData":[TD([[makeQuery(id+"F6.imprint","IMPRINT",EDGE,{"derivedFrom":sQuery(id+"F6.wireOp",EDGE,"E81")}),-1.0]])]});
            var Q43;
            Q43=makeQuery(id+"F6.imprint","IMPRINT",FACE,{"disambiguationData":[TD([[makeQuery(id+"F6.imprint","IMPRINT",EDGE,{"derivedFrom":sQuery(id+"F6.wireOp",EDGE,"E39")}),-1.0]])]});
            var Q44;
            Q44=makeQuery(id+"F6.imprint","IMPRINT",FACE,{"disambiguationData":[TD([[makeQuery(id+"F6.imprint","IMPRINT",EDGE,{"derivedFrom":sQuery(id+"F6.wireOp",EDGE,"E147")}),-1.0]])]});
            var Q45;
            Q45=makeQuery(id+"F6.imprint","IMPRINT",FACE,{"disambiguationData":[TD([[makeQuery(id+"F6.imprint","IMPRINT",EDGE,{"derivedFrom":sQuery(id+"F6.wireOp",EDGE,"E309")}),-1.0]])]});
            var Q46;
            Q46=makeQuery(id+"F6.imprint","IMPRINT",FACE,{"disambiguationData":[TD([[makeQuery(id+"F6.imprint","IMPRINT",EDGE,{"derivedFrom":sQuery(id+"F6.wireOp",EDGE,"E273")}),-1.0]])]});
            var Q47;
            Q47=makeQuery(id+"F6.imprint","IMPRINT",FACE,{"disambiguationData":[TD([[makeQuery(id+"F6.imprint","IMPRINT",EDGE,{"derivedFrom":sQuery(id+"F6.wireOp",EDGE,"E393")}),-1.0]])]});
            var Q48;
            Q48=makeQuery(id+"F6.imprint","IMPRINT",FACE,{"disambiguationData":[TD([[makeQuery(id+"F6.imprint","IMPRINT",EDGE,{"derivedFrom":sQuery(id+"F6.wireOp",EDGE,"E189")}),-1.0]])]});
            var Q49;
            Q49=makeQuery(id+"F6.imprint","IMPRINT",FACE,{"disambiguationData":[TD([[makeQuery(id+"F6.imprint","IMPRINT",EDGE,{"derivedFrom":sQuery(id+"F6.wireOp",EDGE,"E312")}),-1.0]])]});
            var Q50;
            Q50=makeQuery(id+"F6.imprint","IMPRINT",FACE,{"disambiguationData":[TD([[makeQuery(id+"F6.imprint","IMPRINT",EDGE,{"derivedFrom":sQuery(id+"F6.wireOp",EDGE,"E381")}),-1.0]])]});
            var Q51;
            Q51=makeQuery(id+"F6.imprint","IMPRINT",FACE,{"disambiguationData":[TD([[makeQuery(id+"F6.imprint","IMPRINT",EDGE,{"derivedFrom":sQuery(id+"F6.wireOp",EDGE,"E30")}),-1.0]])]});
            var Q52;
            Q52=makeQuery(id+"F6.imprint","IMPRINT",FACE,{"disambiguationData":[TD([[makeQuery(id+"F6.imprint","IMPRINT",EDGE,{"derivedFrom":sQuery(id+"F6.wireOp",EDGE,"E216")}),-1.0]])]});
            var Q53;
            Q53=makeQuery(id+"F6.imprint","IMPRINT",FACE,{"disambiguationData":[TD([[makeQuery(id+"F6.imprint","IMPRINT",EDGE,{"derivedFrom":sQuery(id+"F6.wireOp",EDGE,"E333")}),-1.0]])]});
            var Q54;
            Q54=makeQuery(id+"F6.imprint","IMPRINT",FACE,{"disambiguationData":[TD([[makeQuery(id+"F6.imprint","IMPRINT",EDGE,{"derivedFrom":sQuery(id+"F6.wireOp",EDGE,"E222")}),-1.0]])]});
            var Q55;
            Q55=makeQuery(id+"F6.imprint","IMPRINT",FACE,{"disambiguationData":[TD([[makeQuery(id+"F6.imprint","IMPRINT",EDGE,{"derivedFrom":sQuery(id+"F6.wireOp",EDGE,"E183")}),-1.0]])]});
            var Q56;
            Q56=makeQuery(id+"F6.imprint","IMPRINT",FACE,{"disambiguationData":[TD([[makeQuery(id+"F6.imprint","IMPRINT",EDGE,{"derivedFrom":sQuery(id+"F6.wireOp",EDGE,"E429")}),-1.0]])]});
            var Q57;
            Q57=makeQuery(id+"F6.imprint","IMPRINT",FACE,{"disambiguationData":[TD([[makeQuery(id+"F6.imprint","IMPRINT",EDGE,{"derivedFrom":sQuery(id+"F6.wireOp",EDGE,"E21")}),-1.0]])]});
            var Q58;
            Q58=makeQuery(id+"F6.imprint","IMPRINT",FACE,{"disambiguationData":[TD([[makeQuery(id+"F6.imprint","IMPRINT",EDGE,{"derivedFrom":sQuery(id+"F6.wireOp",EDGE,"E432")}),-1.0]])]});
            var Q59;
            Q59=makeQuery(id+"F6.imprint","IMPRINT",FACE,{"disambiguationData":[TD([[makeQuery(id+"F6.imprint","IMPRINT",EDGE,{"derivedFrom":sQuery(id+"F6.wireOp",EDGE,"E303")}),-1.0]])]});
            var Q60;
            Q60=makeQuery(id+"F6.imprint","IMPRINT",FACE,{"disambiguationData":[TD([[makeQuery(id+"F6.imprint","IMPRINT",EDGE,{"derivedFrom":sQuery(id+"F6.wireOp",EDGE,"E69")}),-1.0]])]});
            var Q61;
            Q61=makeQuery(id+"F6.imprint","IMPRINT",FACE,{"disambiguationData":[TD([[makeQuery(id+"F6.imprint","IMPRINT",EDGE,{"derivedFrom":sQuery(id+"F6.wireOp",EDGE,"E159")}),-1.0]])]});
            var Q62;
            Q62=makeQuery(id+"F6.imprint","IMPRINT",FACE,{"disambiguationData":[TD([[makeQuery(id+"F6.imprint","IMPRINT",EDGE,{"derivedFrom":sQuery(id+"F6.wireOp",EDGE,"E327")}),-1.0]])]});
            var Q63;
            Q63=makeQuery(id+"F6.imprint","IMPRINT",FACE,{"disambiguationData":[TD([[makeQuery(id+"F6.imprint","IMPRINT",EDGE,{"derivedFrom":sQuery(id+"F6.wireOp",EDGE,"E105")}),-1.0]])]});
            var Q64;
            Q64=makeQuery(id+"F6.imprint","IMPRINT",FACE,{"disambiguationData":[TD([[makeQuery(id+"F6.imprint","IMPRINT",EDGE,{"derivedFrom":sQuery(id+"F6.wireOp",EDGE,"E48")}),-1.0]])]});
            var Q65;
            Q65=makeQuery(id+"F6.imprint","IMPRINT",FACE,{"disambiguationData":[TD([[makeQuery(id+"F6.imprint","IMPRINT",EDGE,{"derivedFrom":sQuery(id+"F6.wireOp",EDGE,"E210")}),-1.0]])]});
            var Q66;
            Q66=makeQuery(id+"F6.imprint","IMPRINT",FACE,{"disambiguationData":[TD([[makeQuery(id+"F6.imprint","IMPRINT",EDGE,{"derivedFrom":sQuery(id+"F6.wireOp",EDGE,"E117")}),-1.0]])]});
            var Q67;
            Q67=makeQuery(id+"F6.imprint","IMPRINT",FACE,{"disambiguationData":[TD([[makeQuery(id+"F6.imprint","IMPRINT",EDGE,{"derivedFrom":sQuery(id+"F6.wireOp",EDGE,"E192")}),-1.0]])]});
            var Q68;
            Q68=makeQuery(id+"F6.imprint","IMPRINT",FACE,{"disambiguationData":[TD([[makeQuery(id+"F6.imprint","IMPRINT",EDGE,{"derivedFrom":sQuery(id+"F6.wireOp",EDGE,"E87")}),-1.0]])]});
            var Q69;
            Q69=makeQuery(id+"F6.imprint","IMPRINT",FACE,{"disambiguationData":[TD([[makeQuery(id+"F6.imprint","IMPRINT",EDGE,{"derivedFrom":sQuery(id+"F6.wireOp",EDGE,"E123")}),-1.0]])]});
            var Q70;
            Q70=makeQuery(id+"F6.imprint","IMPRINT",FACE,{"disambiguationData":[TD([[makeQuery(id+"F6.imprint","IMPRINT",EDGE,{"derivedFrom":sQuery(id+"F6.wireOp",EDGE,"E372")}),-1.0]])]});
            var Q71;
            Q71=makeQuery(id+"F6.imprint","IMPRINT",FACE,{"disambiguationData":[TD([[makeQuery(id+"F6.imprint","IMPRINT",EDGE,{"derivedFrom":sQuery(id+"F6.wireOp",EDGE,"E204")}),-1.0]])]});
            var Q72;
            Q72=makeQuery(id+"F6.imprint","IMPRINT",FACE,{"disambiguationData":[TD([[makeQuery(id+"F6.imprint","IMPRINT",EDGE,{"derivedFrom":sQuery(id+"F6.wireOp",EDGE,"E156")}),-1.0]])]});
            var Q73;
            Q73=makeQuery(id+"F6.imprint","IMPRINT",FACE,{"disambiguationData":[TD([[makeQuery(id+"F6.imprint","IMPRINT",EDGE,{"derivedFrom":sQuery(id+"F6.wireOp",EDGE,"E306")}),-1.0]])]});
            var Q74;
            Q74=makeQuery(id+"F6.imprint","IMPRINT",FACE,{"disambiguationData":[TD([[makeQuery(id+"F6.imprint","IMPRINT",EDGE,{"derivedFrom":sQuery(id+"F6.wireOp",EDGE,"E462")}),-1.0]])]});
            var Q75;
            Q75=makeQuery(id+"F6.imprint","IMPRINT",FACE,{"disambiguationData":[TD([[makeQuery(id+"F6.imprint","IMPRINT",EDGE,{"derivedFrom":sQuery(id+"F6.wireOp",EDGE,"E387")}),-1.0]])]});
            var Q76;
            Q76=makeQuery(id+"F6.imprint","IMPRINT",FACE,{"disambiguationData":[TD([[makeQuery(id+"F6.imprint","IMPRINT",EDGE,{"derivedFrom":sQuery(id+"F6.wireOp",EDGE,"E198")}),-1.0]])]});
            var Q77;
            Q77=makeQuery(id+"F6.imprint","IMPRINT",FACE,{"disambiguationData":[TD([[makeQuery(id+"F6.imprint","IMPRINT",EDGE,{"derivedFrom":sQuery(id+"F6.wireOp",EDGE,"E255")}),-1.0]])]});
            var Q78;
            Q78=makeQuery(id+"F6.imprint","IMPRINT",FACE,{"disambiguationData":[TD([[makeQuery(id+"F6.imprint","IMPRINT",EDGE,{"derivedFrom":sQuery(id+"F6.wireOp",EDGE,"E276")}),-1.0]])]});
            var Q79;
            Q79=makeQuery(id+"F6.imprint","IMPRINT",FACE,{"disambiguationData":[TD([[makeQuery(id+"F6.imprint","IMPRINT",EDGE,{"derivedFrom":sQuery(id+"F6.wireOp",EDGE,"E27")}),-1.0]])]});
            var Q80;
            Q80=makeQuery(id+"F6.imprint","IMPRINT",FACE,{"disambiguationData":[TD([[makeQuery(id+"F6.imprint","IMPRINT",EDGE,{"derivedFrom":sQuery(id+"F6.wireOp",EDGE,"E72")}),-1.0]])]});
            var Q81;
            Q81=makeQuery(id+"F6.imprint","IMPRINT",FACE,{"disambiguationData":[TD([[makeQuery(id+"F6.imprint","IMPRINT",EDGE,{"derivedFrom":sQuery(id+"F6.wireOp",EDGE,"E135")}),-1.0]])]});
            var Q82;
            Q82=makeQuery(id+"F6.imprint","IMPRINT",FACE,{"disambiguationData":[TD([[makeQuery(id+"F6.imprint","IMPRINT",EDGE,{"derivedFrom":sQuery(id+"F6.wireOp",EDGE,"E399")}),-1.0]])]});
            var Q83;
            Q83=makeQuery(id+"F6.imprint","IMPRINT",FACE,{"disambiguationData":[TD([[makeQuery(id+"F6.imprint","IMPRINT",EDGE,{"derivedFrom":sQuery(id+"F6.wireOp",EDGE,"E180")}),-1.0]])]});
            var Q84;
            Q84=makeQuery(id+"F6.imprint","IMPRINT",FACE,{"disambiguationData":[TD([[makeQuery(id+"F6.imprint","IMPRINT",EDGE,{"derivedFrom":sQuery(id+"F6.wireOp",EDGE,"E264")}),-1.0]])]});
            var Q85;
            Q85=makeQuery(id+"F6.imprint","IMPRINT",FACE,{"disambiguationData":[TD([[makeQuery(id+"F6.imprint","IMPRINT",EDGE,{"derivedFrom":sQuery(id+"F6.wireOp",EDGE,"E129")}),-1.0]])]});
            var Q86;
            Q86=makeQuery(id+"F6.imprint","IMPRINT",FACE,{"disambiguationData":[TD([[makeQuery(id+"F6.imprint","IMPRINT",EDGE,{"derivedFrom":sQuery(id+"F6.wireOp",EDGE,"E102")}),-1.0]])]});
            var Q87;
            Q87=makeQuery(id+"F6.imprint","IMPRINT",FACE,{"disambiguationData":[TD([[makeQuery(id+"F6.imprint","IMPRINT",EDGE,{"derivedFrom":sQuery(id+"F6.wireOp",EDGE,"E63")}),-1.0]])]});
            var Q88;
            Q88=makeQuery(id+"F6.imprint","IMPRINT",FACE,{"disambiguationData":[TD([[makeQuery(id+"F6.imprint","IMPRINT",EDGE,{"derivedFrom":sQuery(id+"F6.wireOp",EDGE,"E324")}),-1.0]])]});
            var Q89;
            Q89=makeQuery(id+"F6.imprint","IMPRINT",FACE,{"disambiguationData":[TD([[makeQuery(id+"F6.imprint","IMPRINT",EDGE,{"derivedFrom":sQuery(id+"F6.wireOp",EDGE,"E453")}),-1.0]])]});
            var Q90;
            Q90=makeQuery(id+"F6.imprint","IMPRINT",FACE,{"disambiguationData":[TD([[makeQuery(id+"F6.imprint","IMPRINT",EDGE,{"derivedFrom":sQuery(id+"F6.wireOp",EDGE,"E483")}),-1.0]])]});
            var Q91;
            Q91=makeQuery(id+"F6.imprint","IMPRINT",FACE,{"disambiguationData":[TD([[makeQuery(id+"F6.imprint","IMPRINT",EDGE,{"derivedFrom":sQuery(id+"F6.wireOp",EDGE,"E228")}),-1.0]])]});
            var Q92;
            Q92=makeQuery(id+"F6.imprint","IMPRINT",FACE,{"disambiguationData":[TD([[makeQuery(id+"F6.imprint","IMPRINT",EDGE,{"derivedFrom":sQuery(id+"F6.wireOp",EDGE,"E84")}),-1.0]])]});
            var Q93;
            Q93=makeQuery(id+"F6.imprint","IMPRINT",FACE,{"disambiguationData":[TD([[makeQuery(id+"F6.imprint","IMPRINT",EDGE,{"derivedFrom":sQuery(id+"F6.wireOp",EDGE,"E423")}),-1.0]])]});
            var Q94;
            Q94=makeQuery(id+"F6.imprint","IMPRINT",FACE,{"disambiguationData":[TD([[makeQuery(id+"F6.imprint","IMPRINT",EDGE,{"derivedFrom":sQuery(id+"F6.wireOp",EDGE,"E195")}),-1.0]])]});
            var Q95;
            Q95=makeQuery(id+"F6.imprint","IMPRINT",FACE,{"disambiguationData":[TD([[makeQuery(id+"F6.imprint","IMPRINT",EDGE,{"derivedFrom":sQuery(id+"F6.wireOp",EDGE,"E270")}),-1.0]])]});
            var Q96;
            Q96=makeQuery(id+"F6.imprint","IMPRINT",FACE,{"disambiguationData":[TD([[makeQuery(id+"F6.imprint","IMPRINT",EDGE,{"derivedFrom":sQuery(id+"F6.wireOp",EDGE,"E186")}),-1.0]])]});
            var Q97;
            Q97=makeQuery(id+"F6.imprint","IMPRINT",FACE,{"disambiguationData":[TD([[makeQuery(id+"F6.imprint","IMPRINT",EDGE,{"derivedFrom":sQuery(id+"F6.wireOp",EDGE,"E99")}),-1.0]])]});
            var Q98;
            Q98=makeQuery(id+"F6.imprint","IMPRINT",FACE,{"disambiguationData":[TD([[makeQuery(id+"F6.imprint","IMPRINT",EDGE,{"derivedFrom":sQuery(id+"F6.wireOp",EDGE,"E42")}),-1.0]])]});
            var Q99;
            Q99=makeQuery(id+"F6.imprint","IMPRINT",FACE,{"disambiguationData":[TD([[makeQuery(id+"F6.imprint","IMPRINT",EDGE,{"derivedFrom":sQuery(id+"F6.wireOp",EDGE,"E321")}),-1.0]])]});
            var Q100;
            Q100=makeQuery(id+"F6.imprint","IMPRINT",FACE,{"disambiguationData":[TD([[makeQuery(id+"F6.imprint","IMPRINT",EDGE,{"derivedFrom":sQuery(id+"F6.wireOp",EDGE,"E174")}),-1.0]])]});
            var Q101;
            Q101=makeQuery(id+"F6.imprint","IMPRINT",FACE,{"disambiguationData":[TD([[makeQuery(id+"F6.imprint","IMPRINT",EDGE,{"derivedFrom":sQuery(id+"F6.wireOp",EDGE,"E96")}),-1.0]])]});
            var Q102;
            Q102=makeQuery(id+"F6.imprint","IMPRINT",FACE,{"disambiguationData":[TD([[makeQuery(id+"F6.imprint","IMPRINT",EDGE,{"derivedFrom":sQuery(id+"F6.wireOp",EDGE,"E318")}),-1.0]])]});
            var Q103;
            Q103=makeQuery(id+"F6.imprint","IMPRINT",FACE,{"disambiguationData":[TD([[makeQuery(id+"F6.imprint","IMPRINT",EDGE,{"derivedFrom":sQuery(id+"F6.wireOp",EDGE,"E486")}),-1.0]])]});
            var Q104;
            Q104=makeQuery(id+"F6.imprint","IMPRINT",FACE,{"disambiguationData":[TD([[makeQuery(id+"F6.imprint","IMPRINT",EDGE,{"derivedFrom":sQuery(id+"F6.wireOp",EDGE,"E459")}),-1.0]])]});
            var Q105;
            Q105=makeQuery(id+"F6.imprint","IMPRINT",FACE,{"disambiguationData":[TD([[makeQuery(id+"F6.imprint","IMPRINT",EDGE,{"derivedFrom":sQuery(id+"F6.wireOp",EDGE,"E108")}),-1.0]])]});
            var Q106;
            Q106=makeQuery(id+"F6.imprint","IMPRINT",FACE,{"disambiguationData":[TD([[makeQuery(id+"F6.imprint","IMPRINT",EDGE,{"derivedFrom":sQuery(id+"F6.wireOp",EDGE,"E261")}),-1.0]])]});
            var Q107;
            Q107=makeQuery(id+"F6.imprint","IMPRINT",FACE,{"disambiguationData":[TD([[makeQuery(id+"F6.imprint","IMPRINT",EDGE,{"derivedFrom":sQuery(id+"F6.wireOp",EDGE,"E144")}),-1.0]])]});
            var Q108;
            Q108=makeQuery(id+"F6.imprint","IMPRINT",FACE,{"disambiguationData":[TD([[makeQuery(id+"F6.imprint","IMPRINT",EDGE,{"derivedFrom":sQuery(id+"F6.wireOp",EDGE,"E171")}),-1.0]])]});
            var Q109;
            Q109=makeQuery(id+"F6.imprint","IMPRINT",FACE,{"disambiguationData":[TD([[makeQuery(id+"F6.imprint","IMPRINT",EDGE,{"derivedFrom":sQuery(id+"F6.wireOp",EDGE,"E6")}),-1.0]])]});
            var Q110;
            Q110=makeQuery(id+"F6.imprint","IMPRINT",FACE,{"disambiguationData":[TD([[makeQuery(id+"F6.imprint","IMPRINT",EDGE,{"derivedFrom":sQuery(id+"F6.wireOp",EDGE,"E9")}),-1.0]])]});
            var Q111;
            Q111=makeQuery(id+"F6.imprint","IMPRINT",FACE,{"disambiguationData":[TD([[makeQuery(id+"F6.imprint","IMPRINT",EDGE,{"derivedFrom":sQuery(id+"F6.wireOp",EDGE,"E219")}),-1.0]])]});
            var Q112;
            Q112=makeQuery(id+"F6.imprint","IMPRINT",FACE,{"disambiguationData":[TD([[makeQuery(id+"F6.imprint","IMPRINT",EDGE,{"derivedFrom":sQuery(id+"F6.wireOp",EDGE,"E225")}),-1.0]])]});
            var Q113;
            Q113=makeQuery(id+"F6.imprint","IMPRINT",FACE,{"disambiguationData":[TD([[makeQuery(id+"F6.imprint","IMPRINT",EDGE,{"derivedFrom":sQuery(id+"F6.wireOp",EDGE,"E279")}),-1.0]])]});
            var Q114;
            Q114=makeQuery(id+"F6.imprint","IMPRINT",FACE,{"disambiguationData":[TD([[makeQuery(id+"F6.imprint","IMPRINT",EDGE,{"derivedFrom":sQuery(id+"F6.wireOp",EDGE,"E66")}),-1.0]])]});
            var Q115;
            Q115=makeQuery(id+"F6.imprint","IMPRINT",FACE,{"disambiguationData":[TD([[makeQuery(id+"F6.imprint","IMPRINT",EDGE,{"derivedFrom":sQuery(id+"F6.wireOp",EDGE,"E51")}),-1.0]])]});
            var Q116;
            Q116=makeQuery(id+"F6.imprint","IMPRINT",FACE,{"disambiguationData":[TD([[makeQuery(id+"F6.imprint","IMPRINT",EDGE,{"derivedFrom":sQuery(id+"F6.wireOp",EDGE,"E252")}),-1.0]])]});
            var Q117;
            Q117=makeQuery(id+"F6.imprint","IMPRINT",FACE,{"disambiguationData":[TD([[makeQuery(id+"F6.imprint","IMPRINT",EDGE,{"derivedFrom":sQuery(id+"F6.wireOp",EDGE,"E153")}),-1.0]])]});
            var Q118;
            Q118=makeQuery(id+"F6.imprint","IMPRINT",FACE,{"disambiguationData":[TD([[makeQuery(id+"F6.imprint","IMPRINT",EDGE,{"derivedFrom":sQuery(id+"F6.wireOp",EDGE,"E258")}),-1.0]])]});
            var Q119;
            Q119=makeQuery(id+"F6.imprint","IMPRINT",FACE,{"disambiguationData":[TD([[makeQuery(id+"F6.imprint","IMPRINT",EDGE,{"derivedFrom":sQuery(id+"F6.wireOp",EDGE,"E246")}),-1.0]])]});
            var Q120;
            Q120=makeQuery(id+"F6.imprint","IMPRINT",FACE,{"disambiguationData":[TD([[makeQuery(id+"F6.imprint","IMPRINT",EDGE,{"derivedFrom":sQuery(id+"F6.wireOp",EDGE,"E60")}),-1.0]])]});
            var Q121;
            Q121=makeQuery(id+"F6.imprint","IMPRINT",FACE,{"disambiguationData":[TD([[makeQuery(id+"F6.imprint","IMPRINT",EDGE,{"derivedFrom":sQuery(id+"F6.wireOp",EDGE,"E201")}),-1.0]])]});
            var Q122;
            Q122=makeQuery(id+"F6.imprint","IMPRINT",FACE,{"disambiguationData":[TD([[makeQuery(id+"F6.imprint","IMPRINT",EDGE,{"derivedFrom":sQuery(id+"F6.wireOp",EDGE,"E132")}),-1.0]])]});
            var Q123;
            Q123=makeQuery(id+"F6.imprint","IMPRINT",FACE,{"disambiguationData":[TD([[makeQuery(id+"F6.imprint","IMPRINT",EDGE,{"derivedFrom":sQuery(id+"F6.wireOp",EDGE,"E78")}),-1.0]])]});
            var Q124;
            Q124=makeQuery(id+"F6.imprint","IMPRINT",FACE,{"disambiguationData":[TD([[makeQuery(id+"F6.imprint","IMPRINT",EDGE,{"derivedFrom":sQuery(id+"F6.wireOp",EDGE,"E435")}),-1.0]])]});
            var Q125;
            Q125=makeQuery(id+"F6.imprint","IMPRINT",FACE,{"disambiguationData":[TD([[makeQuery(id+"F6.imprint","IMPRINT",EDGE,{"derivedFrom":sQuery(id+"F6.wireOp",EDGE,"E240")}),-1.0]])]});
            var Q126;
            Q126=makeQuery(id+"F6.imprint","IMPRINT",FACE,{"disambiguationData":[TD([[makeQuery(id+"F6.imprint","IMPRINT",EDGE,{"derivedFrom":sQuery(id+"F6.wireOp",EDGE,"E234")}),-1.0]])]});
            var Q127;
            Q127=makeQuery(id+"F6.imprint","IMPRINT",FACE,{"disambiguationData":[TD([[makeQuery(id+"F6.imprint","IMPRINT",EDGE,{"derivedFrom":sQuery(id+"F6.wireOp",EDGE,"E465")}),-1.0]])]});
            var Q128;
            Q128=makeQuery(id+"F6.imprint","IMPRINT",FACE,{"disambiguationData":[TD([[makeQuery(id+"F6.imprint","IMPRINT",EDGE,{"derivedFrom":sQuery(id+"F6.wireOp",EDGE,"E243")}),-1.0]])]});
            var Q129;
            Q129=makeQuery(id+"F6.imprint","IMPRINT",FACE,{"disambiguationData":[TD([[makeQuery(id+"F6.imprint","IMPRINT",EDGE,{"derivedFrom":sQuery(id+"F6.wireOp",EDGE,"E339")}),-1.0]])]});
            var Q130;
            Q130=makeQuery(id+"F6.imprint","IMPRINT",FACE,{"disambiguationData":[TD([[makeQuery(id+"F6.imprint","IMPRINT",EDGE,{"derivedFrom":sQuery(id+"F6.wireOp",EDGE,"E501")}),-1.0]])]});
            var Q131;
            Q131=makeQuery(id+"F6.imprint","IMPRINT",FACE,{"disambiguationData":[TD([[makeQuery(id+"F6.imprint","IMPRINT",EDGE,{"derivedFrom":sQuery(id+"F6.wireOp",EDGE,"E237")}),-1.0]])]});
            var Q132;
            Q132=makeQuery(id+"F6.imprint","IMPRINT",FACE,{"disambiguationData":[TD([[makeQuery(id+"F6.imprint","IMPRINT",EDGE,{"derivedFrom":sQuery(id+"F6.wireOp",EDGE,"E450")}),-1.0]])]});
            var Q133;
            Q133=makeQuery(id+"F6.imprint","IMPRINT",FACE,{"disambiguationData":[TD([[makeQuery(id+"F6.imprint","IMPRINT",EDGE,{"derivedFrom":sQuery(id+"F6.wireOp",EDGE,"E414")}),-1.0]])]});
            extrude(context, id + "F7", {"entities" : qUnion([Q0, Q1, Q2, Q3, Q4, Q5, Q6, Q7, Q8, Q9, Q10, Q11, Q12, Q13, Q14, Q15, Q16, Q17, Q18, Q19, Q20, Q21, Q22, Q23, Q24, Q25, Q26, Q27, Q28, Q29, Q30, Q31, Q32, Q33, Q34, Q35, Q36, Q37, Q38, Q39, Q40, Q41, Q42, Q43, Q44, Q45, Q46, Q47, Q48, Q49, Q50, Q51, Q52, Q53, Q54, Q55, Q56, Q57, Q58, Q59, Q60, Q61, Q62, Q63, Q64, Q65, Q66, Q67, Q68, Q69, Q70, Q71, Q72, Q73, Q74, Q75, Q76, Q77, Q78, Q79, Q80, Q81, Q82, Q83, Q84, Q85, Q86, Q87, Q88, Q89, Q90, Q91, Q92, Q93, Q94, Q95, Q96, Q97, Q98, Q99, Q100, Q101, Q102, Q103, Q104, Q105, Q106, Q107, Q108, Q109, Q110, Q111, Q112, Q113, Q114, Q115, Q116, Q117, Q118, Q119, Q120, Q121, Q122, Q123, Q124, Q125, Q126, Q127, Q128, Q129, Q130, Q131, Q132, Q133]), "operationType" : NewBodyOperationType.REMOVE, "oppositeDirection" : true, "depth" : 3 * mm, "offsetDistance" : 25 * mm});
        }
    });
